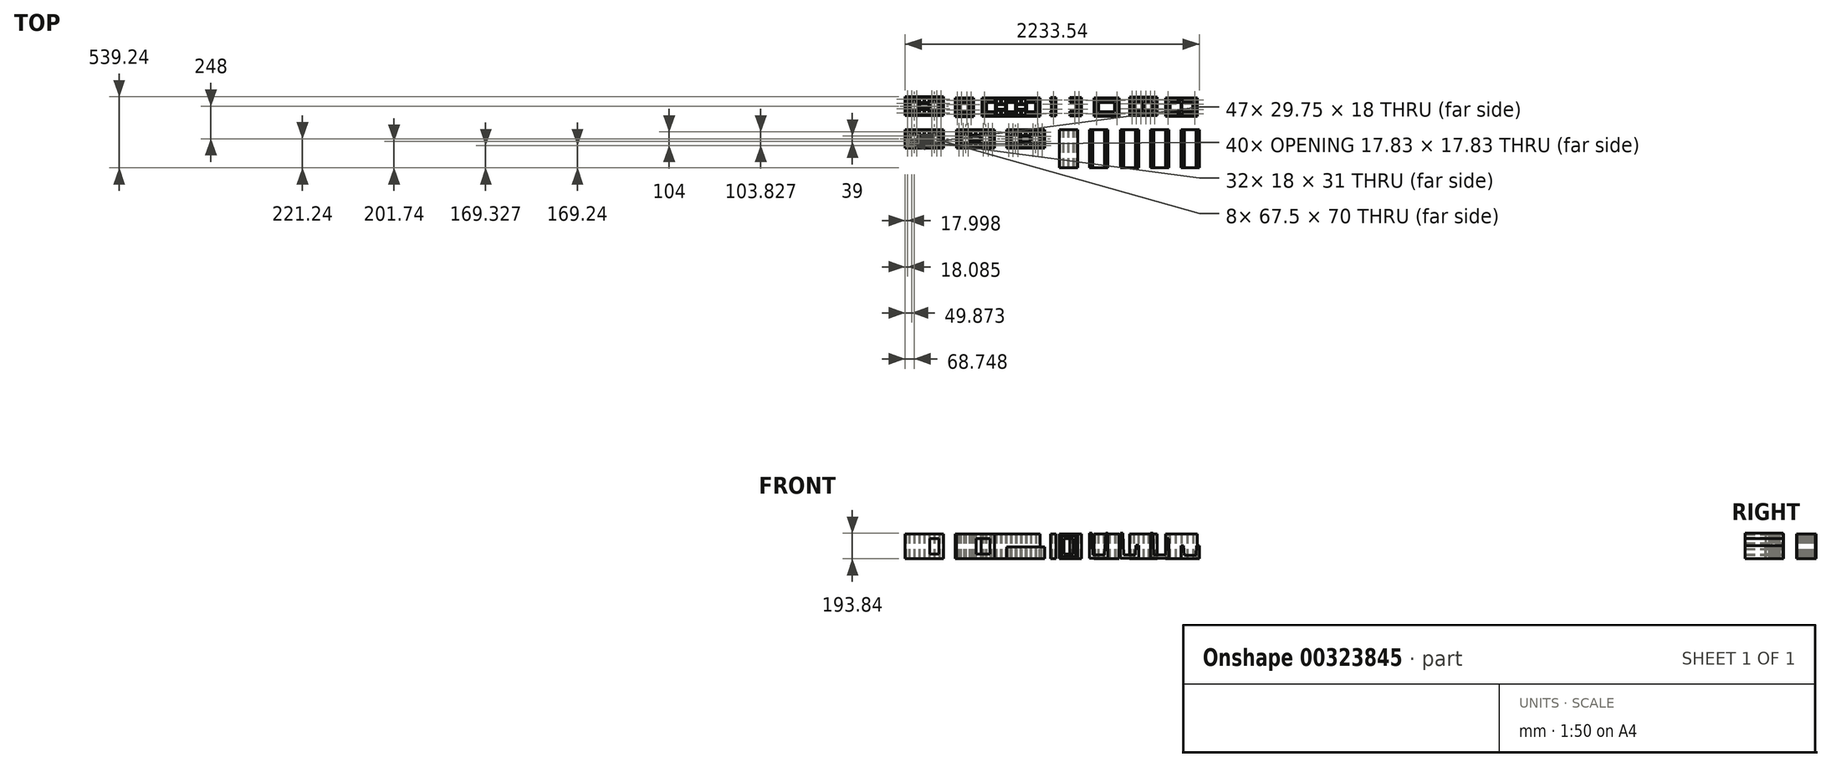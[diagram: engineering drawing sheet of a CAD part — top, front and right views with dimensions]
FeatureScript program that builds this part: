
annotation { "Feature Type Name" : "Feature", "Feature Type Description" : "" }
export const myFeature = defineFeature(function(context is Context, id is Id, definition is map)
    precondition{}
    {
        {
            var Q0;
            Q0=qCreatedBy(makeId("Top.planeOp"),FACE);
            var sketch = newSketch(context, id + "F0", { "sketchPlane" : qUnion([Q0])});
            skLineSegment(sketch, "E0", {"start": v(-1124.68, 173) * mm, "end": v(-1124.68, 33) * mm});
            skLineSegment(sketch, "E1", {"start": v(-1124.68, 33) * mm, "end": v(-834.68, 33) * mm});
            skLineSegment(sketch, "E2", {"start": v(-834.68, 33) * mm, "end": v(-834.68, 173) * mm});
            skLineSegment(sketch, "E3", {"start": v(-834.68, 173) * mm, "end": v(-1124.68, 173) * mm});
            skLineSegment(sketch, "E4", {"start": v(-1089.68, 164) * mm, "end": v(-1089.68, 146) * mm});
            skLineSegment(sketch, "E5", {"start": v(-1089.68, 146) * mm, "end": v(-1059.93, 146) * mm});
            skLineSegment(sketch, "E6", {"start": v(-1059.93, 146) * mm, "end": v(-1059.93, 164) * mm});
            skLineSegment(sketch, "E7", {"start": v(-1059.93, 164) * mm, "end": v(-1089.68, 164) * mm});
            skLineSegment(sketch, "E8", {"start": v(-1051.93, 164) * mm, "end": v(-1051.93, 146) * mm});
            skLineSegment(sketch, "E9", {"start": v(-1051.93, 146) * mm, "end": v(-1022.18, 146) * mm});
            skLineSegment(sketch, "E10", {"start": v(-1022.18, 146) * mm, "end": v(-1022.18, 164) * mm});
            skLineSegment(sketch, "E11", {"start": v(-1022.18, 164) * mm, "end": v(-1051.93, 164) * mm});
            skLineSegment(sketch, "E12", {"start": v(-1014.18, 164) * mm, "end": v(-1014.18, 129) * mm});
            skLineSegment(sketch, "E13", {"start": v(-1014.18, 129) * mm, "end": v(-983.68, 129) * mm});
            skLineSegment(sketch, "E14", {"start": v(-983.68, 129) * mm, "end": v(-983.68, 164) * mm});
            skLineSegment(sketch, "E15", {"start": v(-983.68, 164) * mm, "end": v(-1014.18, 164) * mm});
            skLineSegment(sketch, "E16", {"start": v(-975.68, 164) * mm, "end": v(-975.68, 129) * mm});
            skLineSegment(sketch, "E17", {"start": v(-975.68, 129) * mm, "end": v(-945.18, 129) * mm});
            skLineSegment(sketch, "E18", {"start": v(-945.18, 129) * mm, "end": v(-945.18, 164) * mm});
            skLineSegment(sketch, "E19", {"start": v(-945.18, 164) * mm, "end": v(-975.68, 164) * mm});
            skLineSegment(sketch, "E20", {"start": v(-937.18, 164) * mm, "end": v(-937.18, 146) * mm});
            skLineSegment(sketch, "E21", {"start": v(-937.18, 146) * mm, "end": v(-907.43, 146) * mm});
            skLineSegment(sketch, "E22", {"start": v(-907.43, 146) * mm, "end": v(-907.43, 164) * mm});
            skLineSegment(sketch, "E23", {"start": v(-907.43, 164) * mm, "end": v(-937.18, 164) * mm});
            skLineSegment(sketch, "E24", {"start": v(-899.43, 164) * mm, "end": v(-899.43, 146) * mm});
            skLineSegment(sketch, "E25", {"start": v(-899.43, 146) * mm, "end": v(-869.68, 146) * mm});
            skLineSegment(sketch, "E26", {"start": v(-869.68, 146) * mm, "end": v(-869.68, 164) * mm});
            skLineSegment(sketch, "E27", {"start": v(-869.68, 164) * mm, "end": v(-899.43, 164) * mm});
            skLineSegment(sketch, "E28", {"start": v(-861.68, 138) * mm, "end": v(-861.68, 107) * mm});
            skLineSegment(sketch, "E29", {"start": v(-861.68, 107) * mm, "end": v(-843.68, 107) * mm});
            skLineSegment(sketch, "E30", {"start": v(-843.68, 107) * mm, "end": v(-843.68, 138) * mm});
            skLineSegment(sketch, "E31", {"start": v(-843.68, 138) * mm, "end": v(-861.68, 138) * mm});
            skLineSegment(sketch, "E32", {"start": v(-1089.68, 138) * mm, "end": v(-1089.68, 68) * mm});
            skLineSegment(sketch, "E33", {"start": v(-1089.68, 68) * mm, "end": v(-1022.18, 68) * mm});
            skLineSegment(sketch, "E34", {"start": v(-1022.18, 68) * mm, "end": v(-1022.18, 138) * mm});
            skLineSegment(sketch, "E35", {"start": v(-1022.18, 138) * mm, "end": v(-1089.68, 138) * mm});
            skLineSegment(sketch, "E36", {"start": v(-1115.68, 138) * mm, "end": v(-1115.68, 107) * mm});
            skLineSegment(sketch, "E37", {"start": v(-1115.68, 107) * mm, "end": v(-1097.68, 107) * mm});
            skLineSegment(sketch, "E38", {"start": v(-1097.68, 107) * mm, "end": v(-1097.68, 138) * mm});
            skLineSegment(sketch, "E39", {"start": v(-1097.68, 138) * mm, "end": v(-1115.68, 138) * mm});
            skLineSegment(sketch, "E40", {"start": v(-1115.68, 99) * mm, "end": v(-1115.68, 68) * mm});
            skLineSegment(sketch, "E41", {"start": v(-1115.68, 68) * mm, "end": v(-1097.68, 68) * mm});
            skLineSegment(sketch, "E42", {"start": v(-1097.68, 68) * mm, "end": v(-1097.68, 99) * mm});
            skLineSegment(sketch, "E43", {"start": v(-1097.68, 99) * mm, "end": v(-1115.68, 99) * mm});
            skLineSegment(sketch, "E44", {"start": v(-1089.68, 60) * mm, "end": v(-1089.68, 42) * mm});
            skLineSegment(sketch, "E45", {"start": v(-1089.68, 42) * mm, "end": v(-1059.93, 42) * mm});
            skLineSegment(sketch, "E46", {"start": v(-1059.93, 42) * mm, "end": v(-1059.93, 60) * mm});
            skLineSegment(sketch, "E47", {"start": v(-1059.93, 60) * mm, "end": v(-1089.68, 60) * mm});
            skLineSegment(sketch, "E48", {"start": v(-1051.93, 60) * mm, "end": v(-1051.93, 42) * mm});
            skLineSegment(sketch, "E49", {"start": v(-1051.93, 42) * mm, "end": v(-1022.18, 42) * mm});
            skLineSegment(sketch, "E50", {"start": v(-1022.18, 42) * mm, "end": v(-1022.18, 60) * mm});
            skLineSegment(sketch, "E51", {"start": v(-1022.18, 60) * mm, "end": v(-1051.93, 60) * mm});
            skLineSegment(sketch, "E52", {"start": v(-1014.18, 121) * mm, "end": v(-1014.18, 85) * mm});
            skLineSegment(sketch, "E53", {"start": v(-1014.18, 85) * mm, "end": v(-945.18, 85) * mm});
            skLineSegment(sketch, "E54", {"start": v(-945.18, 85) * mm, "end": v(-945.18, 121) * mm});
            skLineSegment(sketch, "E55", {"start": v(-945.18, 121) * mm, "end": v(-1014.18, 121) * mm});
            skLineSegment(sketch, "E56", {"start": v(-1014.18, 77) * mm, "end": v(-1014.18, 42) * mm});
            skLineSegment(sketch, "E57", {"start": v(-1014.18, 42) * mm, "end": v(-983.68, 42) * mm});
            skLineSegment(sketch, "E58", {"start": v(-983.68, 42) * mm, "end": v(-983.68, 77) * mm});
            skLineSegment(sketch, "E59", {"start": v(-983.68, 77) * mm, "end": v(-1014.18, 77) * mm});
            skLineSegment(sketch, "E60", {"start": v(-975.68, 77) * mm, "end": v(-975.68, 42) * mm});
            skLineSegment(sketch, "E61", {"start": v(-975.68, 42) * mm, "end": v(-945.18, 42) * mm});
            skLineSegment(sketch, "E62", {"start": v(-945.18, 42) * mm, "end": v(-945.18, 77) * mm});
            skLineSegment(sketch, "E63", {"start": v(-945.18, 77) * mm, "end": v(-975.68, 77) * mm});
            skLineSegment(sketch, "E64", {"start": v(-937.18, 138) * mm, "end": v(-937.18, 68) * mm});
            skLineSegment(sketch, "E65", {"start": v(-937.18, 68) * mm, "end": v(-869.68, 68) * mm});
            skLineSegment(sketch, "E66", {"start": v(-869.68, 68) * mm, "end": v(-869.68, 138) * mm});
            skLineSegment(sketch, "E67", {"start": v(-869.68, 138) * mm, "end": v(-937.18, 138) * mm});
            skLineSegment(sketch, "E68", {"start": v(-937.18, 60) * mm, "end": v(-937.18, 42) * mm});
            skLineSegment(sketch, "E69", {"start": v(-937.18, 42) * mm, "end": v(-907.43, 42) * mm});
            skLineSegment(sketch, "E70", {"start": v(-907.43, 42) * mm, "end": v(-907.43, 60) * mm});
            skLineSegment(sketch, "E71", {"start": v(-907.43, 60) * mm, "end": v(-937.18, 60) * mm});
            skLineSegment(sketch, "E72", {"start": v(-899.43, 60) * mm, "end": v(-899.43, 42) * mm});
            skLineSegment(sketch, "E73", {"start": v(-899.43, 42) * mm, "end": v(-869.68, 42) * mm});
            skLineSegment(sketch, "E74", {"start": v(-869.68, 42) * mm, "end": v(-869.68, 60) * mm});
            skLineSegment(sketch, "E75", {"start": v(-869.68, 60) * mm, "end": v(-899.43, 60) * mm});
            skLineSegment(sketch, "E76", {"start": v(-861.68, 99) * mm, "end": v(-861.68, 68) * mm});
            skLineSegment(sketch, "E77", {"start": v(-861.68, 68) * mm, "end": v(-843.68, 68) * mm});
            skLineSegment(sketch, "E78", {"start": v(-843.68, 68) * mm, "end": v(-843.68, 99) * mm});
            skLineSegment(sketch, "E79", {"start": v(-843.68, 99) * mm, "end": v(-861.68, 99) * mm});
            skLineSegment(sketch, "E80", {"start": v(-745.6, 163.5) * mm, "end": v(-745.6, 23.5) * mm});
            skLineSegment(sketch, "E81", {"start": v(-745.6, 23.5) * mm, "end": v(-605.6, 23.5) * mm});
            skLineSegment(sketch, "E82", {"start": v(-605.6, 23.5) * mm, "end": v(-605.6, 163.5) * mm});
            skLineSegment(sketch, "E83", {"start": v(-605.6, 163.5) * mm, "end": v(-745.6, 163.5) * mm});
            skLineSegment(sketch, "E84", {"start": v(-710.6, 154.5) * mm, "end": v(-710.6, 136.5) * mm});
            skLineSegment(sketch, "E85", {"start": v(-710.6, 136.5) * mm, "end": v(-680.86, 136.5) * mm});
            skLineSegment(sketch, "E86", {"start": v(-680.86, 136.5) * mm, "end": v(-680.86, 154.5) * mm});
            skLineSegment(sketch, "E87", {"start": v(-680.86, 154.5) * mm, "end": v(-710.6, 154.5) * mm});
            skLineSegment(sketch, "E88", {"start": v(-670.36, 154.5) * mm, "end": v(-670.36, 136.5) * mm});
            skLineSegment(sketch, "E89", {"start": v(-670.36, 136.5) * mm, "end": v(-640.6, 136.5) * mm});
            skLineSegment(sketch, "E90", {"start": v(-640.6, 136.5) * mm, "end": v(-640.6, 154.5) * mm});
            skLineSegment(sketch, "E91", {"start": v(-640.6, 154.5) * mm, "end": v(-670.36, 154.5) * mm});
            skLineSegment(sketch, "E92", {"start": v(-632.6, 128.5) * mm, "end": v(-632.6, 97.5) * mm});
            skLineSegment(sketch, "E93", {"start": v(-632.6, 97.5) * mm, "end": v(-614.6, 97.5) * mm});
            skLineSegment(sketch, "E94", {"start": v(-614.6, 97.5) * mm, "end": v(-614.6, 128.5) * mm});
            skLineSegment(sketch, "E95", {"start": v(-614.6, 128.5) * mm, "end": v(-632.6, 128.5) * mm});
            skLineSegment(sketch, "E96", {"start": v(-736.6, 128.5) * mm, "end": v(-736.6, 97.5) * mm});
            skLineSegment(sketch, "E97", {"start": v(-736.6, 97.5) * mm, "end": v(-718.6, 97.5) * mm});
            skLineSegment(sketch, "E98", {"start": v(-718.6, 97.5) * mm, "end": v(-718.6, 128.5) * mm});
            skLineSegment(sketch, "E99", {"start": v(-718.6, 128.5) * mm, "end": v(-736.6, 128.5) * mm});
            skLineSegment(sketch, "E100", {"start": v(-736.6, 89.5) * mm, "end": v(-736.6, 58.5) * mm});
            skLineSegment(sketch, "E101", {"start": v(-736.6, 58.5) * mm, "end": v(-718.6, 58.5) * mm});
            skLineSegment(sketch, "E102", {"start": v(-718.6, 58.5) * mm, "end": v(-718.6, 89.5) * mm});
            skLineSegment(sketch, "E103", {"start": v(-718.6, 89.5) * mm, "end": v(-736.6, 89.5) * mm});
            skLineSegment(sketch, "E104", {"start": v(-710.6, 128.5) * mm, "end": v(-710.6, 58.5) * mm});
            skLineSegment(sketch, "E105", {"start": v(-710.6, 58.5) * mm, "end": v(-640.6, 58.5) * mm});
            skLineSegment(sketch, "E106", {"start": v(-640.6, 58.5) * mm, "end": v(-640.6, 128.5) * mm});
            skLineSegment(sketch, "E107", {"start": v(-640.6, 128.5) * mm, "end": v(-710.6, 128.5) * mm});
            skLineSegment(sketch, "E108", {"start": v(-710.6, 50.5) * mm, "end": v(-710.6, 32.5) * mm});
            skLineSegment(sketch, "E109", {"start": v(-710.6, 32.5) * mm, "end": v(-680.86, 32.5) * mm});
            skLineSegment(sketch, "E110", {"start": v(-680.86, 32.5) * mm, "end": v(-680.86, 50.5) * mm});
            skLineSegment(sketch, "E111", {"start": v(-680.86, 50.5) * mm, "end": v(-710.6, 50.5) * mm});
            skLineSegment(sketch, "E112", {"start": v(-670.36, 50.5) * mm, "end": v(-670.36, 32.5) * mm});
            skLineSegment(sketch, "E113", {"start": v(-670.36, 32.5) * mm, "end": v(-640.6, 32.5) * mm});
            skLineSegment(sketch, "E114", {"start": v(-640.6, 32.5) * mm, "end": v(-640.6, 50.5) * mm});
            skLineSegment(sketch, "E115", {"start": v(-640.6, 50.5) * mm, "end": v(-670.36, 50.5) * mm});
            skLineSegment(sketch, "E116", {"start": v(-632.6, 89.5) * mm, "end": v(-632.6, 58.5) * mm});
            skLineSegment(sketch, "E117", {"start": v(-632.6, 58.5) * mm, "end": v(-614.6, 58.5) * mm});
            skLineSegment(sketch, "E118", {"start": v(-614.6, 58.5) * mm, "end": v(-614.6, 89.5) * mm});
            skLineSegment(sketch, "E119", {"start": v(-614.6, 89.5) * mm, "end": v(-632.6, 89.5) * mm});
            skLineSegment(sketch, "E120", {"start": v(-540.95, 165.99) * mm, "end": v(-540.95, 25.99) * mm});
            skLineSegment(sketch, "E121", {"start": v(-100.95, 25.99) * mm, "end": v(-100.95, 165.99) * mm});
            skLineSegment(sketch, "E122", {"start": v(-100.95, 165.99) * mm, "end": v(-540.95, 165.99) * mm});
            skLineSegment(sketch, "E123", {"start": v(-506.14, 156.99) * mm, "end": v(-506.14, 138.99) * mm});
            skLineSegment(sketch, "E124", {"start": v(-506.14, 138.99) * mm, "end": v(-476.56, 138.99) * mm});
            skLineSegment(sketch, "E125", {"start": v(-476.56, 138.99) * mm, "end": v(-476.56, 156.99) * mm});
            skLineSegment(sketch, "E126", {"start": v(-476.56, 156.99) * mm, "end": v(-506.14, 156.99) * mm});
            skLineSegment(sketch, "E127", {"start": v(-468.6, 156.99) * mm, "end": v(-468.6, 138.99) * mm});
            skLineSegment(sketch, "E128", {"start": v(-468.6, 138.99) * mm, "end": v(-439.03, 138.99) * mm});
            skLineSegment(sketch, "E129", {"start": v(-439.03, 138.99) * mm, "end": v(-439.03, 156.99) * mm});
            skLineSegment(sketch, "E130", {"start": v(-439.03, 156.99) * mm, "end": v(-468.6, 156.99) * mm});
            skLineSegment(sketch, "E131", {"start": v(-532, 130.99) * mm, "end": v(-532, 99.99) * mm});
            skLineSegment(sketch, "E132", {"start": v(-532, 99.99) * mm, "end": v(-514.1, 99.99) * mm});
            skLineSegment(sketch, "E133", {"start": v(-514.1, 99.99) * mm, "end": v(-514.1, 130.99) * mm});
            skLineSegment(sketch, "E134", {"start": v(-514.1, 130.99) * mm, "end": v(-532, 130.99) * mm});
            skLineSegment(sketch, "E135", {"start": v(-532, 91.99) * mm, "end": v(-532, 60.99) * mm});
            skLineSegment(sketch, "E136", {"start": v(-532, 60.99) * mm, "end": v(-514.1, 60.99) * mm});
            skLineSegment(sketch, "E137", {"start": v(-514.1, 60.99) * mm, "end": v(-514.1, 91.99) * mm});
            skLineSegment(sketch, "E138", {"start": v(-514.1, 91.99) * mm, "end": v(-532, 91.99) * mm});
            skLineSegment(sketch, "E139", {"start": v(-506.14, 52.99) * mm, "end": v(-506.14, 34.99) * mm});
            skLineSegment(sketch, "E140", {"start": v(-506.14, 34.99) * mm, "end": v(-476.56, 34.99) * mm});
            skLineSegment(sketch, "E141", {"start": v(-476.56, 34.99) * mm, "end": v(-476.56, 52.99) * mm});
            skLineSegment(sketch, "E142", {"start": v(-476.56, 52.99) * mm, "end": v(-506.14, 52.99) * mm});
            skLineSegment(sketch, "E143", {"start": v(-468.6, 52.99) * mm, "end": v(-468.6, 34.99) * mm});
            skLineSegment(sketch, "E144", {"start": v(-468.6, 34.99) * mm, "end": v(-439.03, 34.99) * mm});
            skLineSegment(sketch, "E145", {"start": v(-439.03, 34.99) * mm, "end": v(-439.03, 52.99) * mm});
            skLineSegment(sketch, "E146", {"start": v(-439.03, 52.99) * mm, "end": v(-468.6, 52.99) * mm});
            skLineSegment(sketch, "E147", {"start": v(-431.07, 156.99) * mm, "end": v(-431.07, 121.99) * mm});
            skLineSegment(sketch, "E148", {"start": v(-431.07, 121.99) * mm, "end": v(-400.74, 121.99) * mm});
            skLineSegment(sketch, "E149", {"start": v(-400.74, 121.99) * mm, "end": v(-400.74, 156.99) * mm});
            skLineSegment(sketch, "E150", {"start": v(-400.74, 156.99) * mm, "end": v(-431.07, 156.99) * mm});
            skLineSegment(sketch, "E151", {"start": v(-392.79, 156.99) * mm, "end": v(-392.79, 121.99) * mm});
            skLineSegment(sketch, "E152", {"start": v(-392.79, 121.99) * mm, "end": v(-362.46, 121.99) * mm});
            skLineSegment(sketch, "E153", {"start": v(-362.46, 121.99) * mm, "end": v(-362.46, 156.99) * mm});
            skLineSegment(sketch, "E154", {"start": v(-362.46, 156.99) * mm, "end": v(-392.79, 156.99) * mm});
            skLineSegment(sketch, "E155", {"start": v(-431.07, 113.99) * mm, "end": v(-431.07, 77.99) * mm});
            skLineSegment(sketch, "E156", {"start": v(-431.07, 77.99) * mm, "end": v(-362.46, 77.99) * mm});
            skLineSegment(sketch, "E157", {"start": v(-362.46, 77.99) * mm, "end": v(-362.46, 113.99) * mm});
            skLineSegment(sketch, "E158", {"start": v(-362.46, 113.99) * mm, "end": v(-431.07, 113.99) * mm});
            skLineSegment(sketch, "E159", {"start": v(-431.07, 69.99) * mm, "end": v(-431.07, 34.99) * mm});
            skLineSegment(sketch, "E160", {"start": v(-431.07, 34.99) * mm, "end": v(-400.74, 34.99) * mm});
            skLineSegment(sketch, "E161", {"start": v(-400.74, 34.99) * mm, "end": v(-400.74, 69.99) * mm});
            skLineSegment(sketch, "E162", {"start": v(-400.74, 69.99) * mm, "end": v(-431.07, 69.99) * mm});
            skLineSegment(sketch, "E163", {"start": v(-392.79, 69.99) * mm, "end": v(-392.79, 34.99) * mm});
            skLineSegment(sketch, "E164", {"start": v(-392.79, 34.99) * mm, "end": v(-362.46, 34.99) * mm});
            skLineSegment(sketch, "E165", {"start": v(-362.46, 34.99) * mm, "end": v(-362.46, 69.99) * mm});
            skLineSegment(sketch, "E166", {"start": v(-362.46, 69.99) * mm, "end": v(-392.79, 69.99) * mm});
            skLineSegment(sketch, "E167", {"start": v(-506.14, 130.99) * mm, "end": v(-506.14, 60.99) * mm});
            skLineSegment(sketch, "E168", {"start": v(-506.14, 60.99) * mm, "end": v(-439.03, 60.99) * mm});
            skLineSegment(sketch, "E169", {"start": v(-439.03, 60.99) * mm, "end": v(-439.03, 130.99) * mm});
            skLineSegment(sketch, "E170", {"start": v(-439.03, 130.99) * mm, "end": v(-506.14, 130.99) * mm});
            skLineSegment(sketch, "E171", {"start": v(-354.5, 156.99) * mm, "end": v(-354.5, 138.99) * mm});
            skLineSegment(sketch, "E172", {"start": v(-354.5, 138.99) * mm, "end": v(-324.92, 138.99) * mm});
            skLineSegment(sketch, "E173", {"start": v(-324.92, 138.99) * mm, "end": v(-324.92, 156.99) * mm});
            skLineSegment(sketch, "E174", {"start": v(-324.92, 156.99) * mm, "end": v(-354.5, 156.99) * mm});
            skLineSegment(sketch, "E175", {"start": v(-316.97, 156.99) * mm, "end": v(-316.97, 138.99) * mm});
            skLineSegment(sketch, "E176", {"start": v(-316.97, 138.99) * mm, "end": v(-287.39, 138.99) * mm});
            skLineSegment(sketch, "E177", {"start": v(-287.39, 138.99) * mm, "end": v(-287.39, 156.99) * mm});
            skLineSegment(sketch, "E178", {"start": v(-287.39, 156.99) * mm, "end": v(-316.97, 156.99) * mm});
            skLineSegment(sketch, "E179", {"start": v(-279.43, 156.99) * mm, "end": v(-279.43, 121.99) * mm});
            skLineSegment(sketch, "E180", {"start": v(-279.43, 121.99) * mm, "end": v(-249.1, 121.99) * mm});
            skLineSegment(sketch, "E181", {"start": v(-249.1, 121.99) * mm, "end": v(-249.1, 156.99) * mm});
            skLineSegment(sketch, "E182", {"start": v(-249.1, 156.99) * mm, "end": v(-279.43, 156.99) * mm});
            skLineSegment(sketch, "E183", {"start": v(-241.15, 156.99) * mm, "end": v(-241.15, 121.99) * mm});
            skLineSegment(sketch, "E184", {"start": v(-241.15, 121.99) * mm, "end": v(-210.82, 121.99) * mm});
            skLineSegment(sketch, "E185", {"start": v(-210.82, 121.99) * mm, "end": v(-210.82, 156.99) * mm});
            skLineSegment(sketch, "E186", {"start": v(-210.82, 156.99) * mm, "end": v(-241.15, 156.99) * mm});
            skLineSegment(sketch, "E187", {"start": v(-202.87, 156.99) * mm, "end": v(-202.87, 138.99) * mm});
            skLineSegment(sketch, "E188", {"start": v(-202.87, 138.99) * mm, "end": v(-173.29, 138.99) * mm});
            skLineSegment(sketch, "E189", {"start": v(-173.29, 138.99) * mm, "end": v(-173.29, 156.99) * mm});
            skLineSegment(sketch, "E190", {"start": v(-173.29, 156.99) * mm, "end": v(-202.87, 156.99) * mm});
            skLineSegment(sketch, "E191", {"start": v(-165.33, 156.99) * mm, "end": v(-165.33, 138.99) * mm});
            skLineSegment(sketch, "E192", {"start": v(-165.33, 138.99) * mm, "end": v(-135.75, 138.99) * mm});
            skLineSegment(sketch, "E193", {"start": v(-135.75, 138.99) * mm, "end": v(-135.75, 156.99) * mm});
            skLineSegment(sketch, "E194", {"start": v(-135.75, 156.99) * mm, "end": v(-165.33, 156.99) * mm});
            skLineSegment(sketch, "E195", {"start": v(-354.5, 130.99) * mm, "end": v(-354.5, 60.99) * mm});
            skLineSegment(sketch, "E196", {"start": v(-354.5, 60.99) * mm, "end": v(-287.39, 60.99) * mm});
            skLineSegment(sketch, "E197", {"start": v(-287.39, 60.99) * mm, "end": v(-287.39, 130.99) * mm});
            skLineSegment(sketch, "E198", {"start": v(-287.39, 130.99) * mm, "end": v(-354.5, 130.99) * mm});
            skLineSegment(sketch, "E199", {"start": v(-354.5, 52.99) * mm, "end": v(-354.5, 34.99) * mm});
            skLineSegment(sketch, "E200", {"start": v(-354.5, 34.99) * mm, "end": v(-324.92, 34.99) * mm});
            skLineSegment(sketch, "E201", {"start": v(-324.92, 34.99) * mm, "end": v(-324.92, 52.99) * mm});
            skLineSegment(sketch, "E202", {"start": v(-324.92, 52.99) * mm, "end": v(-354.5, 52.99) * mm});
            skLineSegment(sketch, "E203", {"start": v(-316.97, 52.99) * mm, "end": v(-316.97, 34.99) * mm});
            skLineSegment(sketch, "E204", {"start": v(-316.97, 34.99) * mm, "end": v(-287.39, 34.99) * mm});
            skLineSegment(sketch, "E205", {"start": v(-287.39, 34.99) * mm, "end": v(-287.39, 52.99) * mm});
            skLineSegment(sketch, "E206", {"start": v(-287.39, 52.99) * mm, "end": v(-316.97, 52.99) * mm});
            skLineSegment(sketch, "E207", {"start": v(-279.43, 69.99) * mm, "end": v(-279.43, 34.99) * mm});
            skLineSegment(sketch, "E208", {"start": v(-279.43, 34.99) * mm, "end": v(-249.1, 34.99) * mm});
            skLineSegment(sketch, "E209", {"start": v(-249.1, 34.99) * mm, "end": v(-249.1, 69.99) * mm});
            skLineSegment(sketch, "E210", {"start": v(-249.1, 69.99) * mm, "end": v(-279.43, 69.99) * mm});
            skLineSegment(sketch, "E211", {"start": v(-279.43, 113.99) * mm, "end": v(-279.43, 77.99) * mm});
            skLineSegment(sketch, "E212", {"start": v(-279.43, 77.99) * mm, "end": v(-210.82, 77.99) * mm});
            skLineSegment(sketch, "E213", {"start": v(-210.82, 77.99) * mm, "end": v(-210.82, 113.99) * mm});
            skLineSegment(sketch, "E214", {"start": v(-210.82, 113.99) * mm, "end": v(-279.43, 113.99) * mm});
            skLineSegment(sketch, "E215", {"start": v(-241.15, 69.99) * mm, "end": v(-241.15, 34.99) * mm});
            skLineSegment(sketch, "E216", {"start": v(-241.15, 34.99) * mm, "end": v(-210.82, 34.99) * mm});
            skLineSegment(sketch, "E217", {"start": v(-210.82, 34.99) * mm, "end": v(-210.82, 69.99) * mm});
            skLineSegment(sketch, "E218", {"start": v(-210.82, 69.99) * mm, "end": v(-241.15, 69.99) * mm});
            skLineSegment(sketch, "E219", {"start": v(-202.87, 130.99) * mm, "end": v(-202.87, 60.99) * mm});
            skLineSegment(sketch, "E220", {"start": v(-202.87, 60.99) * mm, "end": v(-135.75, 60.99) * mm});
            skLineSegment(sketch, "E221", {"start": v(-135.75, 60.99) * mm, "end": v(-135.75, 130.99) * mm});
            skLineSegment(sketch, "E222", {"start": v(-135.75, 130.99) * mm, "end": v(-202.87, 130.99) * mm});
            skLineSegment(sketch, "E223", {"start": v(-202.87, 52.99) * mm, "end": v(-202.87, 34.99) * mm});
            skLineSegment(sketch, "E224", {"start": v(-202.87, 34.99) * mm, "end": v(-173.29, 34.99) * mm});
            skLineSegment(sketch, "E225", {"start": v(-173.29, 34.99) * mm, "end": v(-173.29, 52.99) * mm});
            skLineSegment(sketch, "E226", {"start": v(-173.29, 52.99) * mm, "end": v(-202.87, 52.99) * mm});
            skLineSegment(sketch, "E227", {"start": v(-165.33, 52.99) * mm, "end": v(-165.33, 34.99) * mm});
            skLineSegment(sketch, "E228", {"start": v(-165.33, 34.99) * mm, "end": v(-135.75, 34.99) * mm});
            skLineSegment(sketch, "E229", {"start": v(-135.75, 34.99) * mm, "end": v(-135.75, 52.99) * mm});
            skLineSegment(sketch, "E230", {"start": v(-135.75, 52.99) * mm, "end": v(-165.33, 52.99) * mm});
            skLineSegment(sketch, "E231", {"start": v(-127.8, 130.99) * mm, "end": v(-127.8, 99.99) * mm});
            skLineSegment(sketch, "E232", {"start": v(-127.8, 99.99) * mm, "end": v(-109.9, 99.99) * mm});
            skLineSegment(sketch, "E233", {"start": v(-109.9, 99.99) * mm, "end": v(-109.9, 130.99) * mm});
            skLineSegment(sketch, "E234", {"start": v(-109.9, 130.99) * mm, "end": v(-127.8, 130.99) * mm});
            skLineSegment(sketch, "E235", {"start": v(-109.9, 91.99) * mm, "end": v(-109.9, 60.99) * mm});
            skLineSegment(sketch, "E236", {"start": v(-109.9, 60.99) * mm, "end": v(-127.8, 60.99) * mm});
            skLineSegment(sketch, "E237", {"start": v(-127.8, 60.99) * mm, "end": v(-127.8, 91.99) * mm});
            skLineSegment(sketch, "E238", {"start": v(-127.8, 91.99) * mm, "end": v(-109.9, 91.99) * mm});
            skLineSegment(sketch, "E239", {"start": v(-6.9, 133.72) * mm, "end": v(-6.9, 102.72) * mm});
            skLineSegment(sketch, "E240", {"start": v(-6.9, 102.72) * mm, "end": v(11.1, 102.72) * mm});
            skLineSegment(sketch, "E241", {"start": v(11.1, 102.72) * mm, "end": v(11.1, 133.72) * mm});
            skLineSegment(sketch, "E242", {"start": v(11.1, 133.72) * mm, "end": v(-6.9, 133.72) * mm});
            skLineSegment(sketch, "E243", {"start": v(-6.9, 94.72) * mm, "end": v(-6.9, 63.72) * mm});
            skLineSegment(sketch, "E244", {"start": v(-6.9, 63.72) * mm, "end": v(11.1, 63.72) * mm});
            skLineSegment(sketch, "E245", {"start": v(11.1, 63.72) * mm, "end": v(11.1, 94.72) * mm});
            skLineSegment(sketch, "E246", {"start": v(11.1, 94.72) * mm, "end": v(-6.9, 94.72) * mm});
            skLineSegment(sketch, "E247", {"start": v(-19.9, 168.72) * mm, "end": v(20.1, 168.72) * mm});
            skLineSegment(sketch, "E248", {"start": v(20.1, 168.72) * mm, "end": v(20.1, 28.72) * mm});
            skLineSegment(sketch, "E249", {"start": v(20.1, 28.72) * mm, "end": v(-19.9, 28.72) * mm});
            skLineSegment(sketch, "E250", {"start": v(-19.9, 28.72) * mm, "end": v(-19.9, 37.72) * mm});
            skLineSegment(sketch, "E251", {"start": v(-19.9, 37.72) * mm, "end": v(-14.9, 37.72) * mm});
            skLineSegment(sketch, "E252", {"start": v(-14.9, 37.72) * mm, "end": v(-14.9, 55.72) * mm});
            skLineSegment(sketch, "E253", {"start": v(-14.9, 55.72) * mm, "end": v(-19.9, 55.72) * mm});
            skLineSegment(sketch, "E254", {"start": v(-19.9, 55.72) * mm, "end": v(-19.9, 63.72) * mm});
            skLineSegment(sketch, "E255", {"start": v(-19.9, 63.72) * mm, "end": v(-14.9, 63.72) * mm});
            skLineSegment(sketch, "E256", {"start": v(-14.9, 63.72) * mm, "end": v(-14.9, 133.72) * mm});
            skLineSegment(sketch, "E257", {"start": v(-14.9, 133.72) * mm, "end": v(-19.9, 133.72) * mm});
            skLineSegment(sketch, "E258", {"start": v(-19.9, 133.72) * mm, "end": v(-19.9, 141.72) * mm});
            skLineSegment(sketch, "E259", {"start": v(-19.9, 141.72) * mm, "end": v(-14.9, 141.72) * mm});
            skLineSegment(sketch, "E260", {"start": v(-14.9, 141.72) * mm, "end": v(-14.9, 159.72) * mm});
            skLineSegment(sketch, "E261", {"start": v(-14.9, 159.72) * mm, "end": v(-19.9, 159.72) * mm});
            skLineSegment(sketch, "E262", {"start": v(-19.9, 159.72) * mm, "end": v(-19.9, 168.72) * mm});
            skLineSegment(sketch, "E263", {"start": v(123.75, 168) * mm, "end": v(213.75, 168) * mm});
            skLineSegment(sketch, "E264", {"start": v(213.75, 168) * mm, "end": v(213.75, 28) * mm});
            skLineSegment(sketch, "E265", {"start": v(213.75, 28) * mm, "end": v(123.75, 28) * mm});
            skLineSegment(sketch, "E266", {"start": v(123.75, 28) * mm, "end": v(123.75, 37) * mm});
            skLineSegment(sketch, "E267", {"start": v(123.75, 37) * mm, "end": v(141, 37) * mm});
            skLineSegment(sketch, "E268", {"start": v(141, 37) * mm, "end": v(141, 55) * mm});
            skLineSegment(sketch, "E269", {"start": v(141, 55) * mm, "end": v(123.75, 55) * mm});
            skLineSegment(sketch, "E270", {"start": v(123.75, 55) * mm, "end": v(123.75, 63) * mm});
            skLineSegment(sketch, "E271", {"start": v(123.75, 63) * mm, "end": v(178.75, 63) * mm});
            skLineSegment(sketch, "E272", {"start": v(178.75, 63) * mm, "end": v(178.75, 133) * mm});
            skLineSegment(sketch, "E273", {"start": v(178.75, 133) * mm, "end": v(123.75, 133) * mm});
            skLineSegment(sketch, "E274", {"start": v(123.75, 133) * mm, "end": v(123.75, 141) * mm});
            skLineSegment(sketch, "E275", {"start": v(123.75, 141) * mm, "end": v(141, 141) * mm});
            skLineSegment(sketch, "E276", {"start": v(141, 141) * mm, "end": v(141, 159) * mm});
            skLineSegment(sketch, "E277", {"start": v(141, 159) * mm, "end": v(123.75, 159) * mm});
            skLineSegment(sketch, "E278", {"start": v(123.75, 159) * mm, "end": v(123.75, 168) * mm});
            skLineSegment(sketch, "E279", {"start": v(149, 159) * mm, "end": v(149, 141) * mm});
            skLineSegment(sketch, "E280", {"start": v(149, 141) * mm, "end": v(178.75, 141) * mm});
            skLineSegment(sketch, "E281", {"start": v(178.75, 141) * mm, "end": v(178.75, 159) * mm});
            skLineSegment(sketch, "E282", {"start": v(178.75, 159) * mm, "end": v(149, 159) * mm});
            skLineSegment(sketch, "E283", {"start": v(186.75, 133) * mm, "end": v(186.75, 102) * mm});
            skLineSegment(sketch, "E284", {"start": v(186.75, 102) * mm, "end": v(204.75, 102) * mm});
            skLineSegment(sketch, "E285", {"start": v(204.75, 102) * mm, "end": v(204.75, 133) * mm});
            skLineSegment(sketch, "E286", {"start": v(204.75, 133) * mm, "end": v(186.75, 133) * mm});
            skLineSegment(sketch, "E287", {"start": v(204.75, 94) * mm, "end": v(204.75, 63) * mm});
            skLineSegment(sketch, "E288", {"start": v(204.75, 63) * mm, "end": v(186.75, 63) * mm});
            skLineSegment(sketch, "E289", {"start": v(186.75, 63) * mm, "end": v(186.75, 94) * mm});
            skLineSegment(sketch, "E290", {"start": v(186.75, 94) * mm, "end": v(204.75, 94) * mm});
            skLineSegment(sketch, "E291", {"start": v(149, 55) * mm, "end": v(149, 37) * mm});
            skLineSegment(sketch, "E292", {"start": v(149, 37) * mm, "end": v(178.75, 37) * mm});
            skLineSegment(sketch, "E293", {"start": v(178.75, 37) * mm, "end": v(178.75, 55) * mm});
            skLineSegment(sketch, "E294", {"start": v(178.75, 55) * mm, "end": v(149, 55) * mm});
            skLineSegment(sketch, "E295", {"start": v(310.8, 164.82) * mm, "end": v(310.8, 24.82) * mm});
            skLineSegment(sketch, "E296", {"start": v(310.8, 24.82) * mm, "end": v(500.8, 24.82) * mm});
            skLineSegment(sketch, "E297", {"start": v(500.8, 24.82) * mm, "end": v(500.8, 164.82) * mm});
            skLineSegment(sketch, "E298", {"start": v(500.8, 164.82) * mm, "end": v(310.8, 164.82) * mm});
            skLineSegment(sketch, "E299", {"start": v(345.8, 155.82) * mm, "end": v(345.8, 137.82) * mm});
            skLineSegment(sketch, "E300", {"start": v(345.8, 137.82) * mm, "end": v(380.46, 137.82) * mm});
            skLineSegment(sketch, "E301", {"start": v(380.46, 137.82) * mm, "end": v(380.46, 155.82) * mm});
            skLineSegment(sketch, "E302", {"start": v(380.46, 155.82) * mm, "end": v(345.8, 155.82) * mm});
            skLineSegment(sketch, "E303", {"start": v(388.46, 155.82) * mm, "end": v(388.46, 137.82) * mm});
            skLineSegment(sketch, "E304", {"start": v(388.46, 137.82) * mm, "end": v(423.13, 137.82) * mm});
            skLineSegment(sketch, "E305", {"start": v(423.13, 137.82) * mm, "end": v(423.13, 155.82) * mm});
            skLineSegment(sketch, "E306", {"start": v(423.13, 155.82) * mm, "end": v(388.46, 155.82) * mm});
            skLineSegment(sketch, "E307", {"start": v(431.13, 137.82) * mm, "end": v(431.13, 155.82) * mm});
            skLineSegment(sketch, "E308", {"start": v(431.13, 155.82) * mm, "end": v(465.8, 155.82) * mm});
            skLineSegment(sketch, "E309", {"start": v(465.8, 155.82) * mm, "end": v(465.8, 137.82) * mm});
            skLineSegment(sketch, "E310", {"start": v(465.8, 137.82) * mm, "end": v(431.13, 137.82) * mm});
            skLineSegment(sketch, "E311", {"start": v(319.8, 129.82) * mm, "end": v(319.8, 99.82) * mm});
            skLineSegment(sketch, "E312", {"start": v(319.8, 99.82) * mm, "end": v(337.8, 99.82) * mm});
            skLineSegment(sketch, "E313", {"start": v(337.8, 99.82) * mm, "end": v(337.8, 129.82) * mm});
            skLineSegment(sketch, "E314", {"start": v(337.8, 129.82) * mm, "end": v(319.8, 129.82) * mm});
            skLineSegment(sketch, "E315", {"start": v(337.8, 89.82) * mm, "end": v(337.8, 59.82) * mm});
            skLineSegment(sketch, "E316", {"start": v(337.8, 59.82) * mm, "end": v(319.8, 59.82) * mm});
            skLineSegment(sketch, "E317", {"start": v(319.8, 59.82) * mm, "end": v(319.8, 89.82) * mm});
            skLineSegment(sketch, "E318", {"start": v(319.8, 89.82) * mm, "end": v(337.8, 89.82) * mm});
            skLineSegment(sketch, "E319", {"start": v(345.8, 51.82) * mm, "end": v(345.8, 33.82) * mm});
            skLineSegment(sketch, "E320", {"start": v(345.8, 33.82) * mm, "end": v(380.46, 33.82) * mm});
            skLineSegment(sketch, "E321", {"start": v(380.46, 33.82) * mm, "end": v(380.46, 51.82) * mm});
            skLineSegment(sketch, "E322", {"start": v(380.46, 51.82) * mm, "end": v(345.8, 51.82) * mm});
            skLineSegment(sketch, "E323", {"start": v(388.46, 33.82) * mm, "end": v(388.46, 51.82) * mm});
            skLineSegment(sketch, "E324", {"start": v(388.46, 51.82) * mm, "end": v(423.13, 51.82) * mm});
            skLineSegment(sketch, "E325", {"start": v(423.13, 51.82) * mm, "end": v(423.13, 33.82) * mm});
            skLineSegment(sketch, "E326", {"start": v(423.13, 33.82) * mm, "end": v(388.46, 33.82) * mm});
            skLineSegment(sketch, "E327", {"start": v(431.13, 51.82) * mm, "end": v(431.13, 33.82) * mm});
            skLineSegment(sketch, "E328", {"start": v(431.13, 33.82) * mm, "end": v(465.8, 33.82) * mm});
            skLineSegment(sketch, "E329", {"start": v(465.8, 33.82) * mm, "end": v(465.8, 51.82) * mm});
            skLineSegment(sketch, "E330", {"start": v(465.8, 51.82) * mm, "end": v(431.13, 51.82) * mm});
            skLineSegment(sketch, "E331", {"start": v(345.8, 129.82) * mm, "end": v(345.8, 59.82) * mm});
            skLineSegment(sketch, "E332", {"start": v(345.8, 59.82) * mm, "end": v(465.8, 59.82) * mm});
            skLineSegment(sketch, "E333", {"start": v(465.8, 59.82) * mm, "end": v(465.8, 129.82) * mm});
            skLineSegment(sketch, "E334", {"start": v(465.8, 129.82) * mm, "end": v(345.8, 129.82) * mm});
            skLineSegment(sketch, "E335", {"start": v(473.8, 129.82) * mm, "end": v(473.8, 99.82) * mm});
            skLineSegment(sketch, "E336", {"start": v(473.8, 99.82) * mm, "end": v(491.8, 99.82) * mm});
            skLineSegment(sketch, "E337", {"start": v(491.8, 99.82) * mm, "end": v(491.8, 129.82) * mm});
            skLineSegment(sketch, "E338", {"start": v(491.8, 129.82) * mm, "end": v(473.8, 129.82) * mm});
            skLineSegment(sketch, "E339", {"start": v(473.8, 89.82) * mm, "end": v(473.8, 59.82) * mm});
            skLineSegment(sketch, "E340", {"start": v(473.8, 59.82) * mm, "end": v(491.8, 59.82) * mm});
            skLineSegment(sketch, "E341", {"start": v(491.8, 59.82) * mm, "end": v(491.8, 89.82) * mm});
            skLineSegment(sketch, "E342", {"start": v(491.8, 89.82) * mm, "end": v(473.8, 89.82) * mm});
            skLineSegment(sketch, "E343", {"start": v(579.39, 171.67) * mm, "end": v(579.39, 31.67) * mm});
            skLineSegment(sketch, "E344", {"start": v(579.39, 31.67) * mm, "end": v(789.39, 31.67) * mm});
            skLineSegment(sketch, "E345", {"start": v(789.39, 31.67) * mm, "end": v(789.39, 171.67) * mm});
            skLineSegment(sketch, "E346", {"start": v(789.39, 171.67) * mm, "end": v(579.39, 171.67) * mm});
            skLineSegment(sketch, "E347", {"start": v(614.39, 162.67) * mm, "end": v(614.39, 144.67) * mm});
            skLineSegment(sketch, "E348", {"start": v(614.39, 144.67) * mm, "end": v(644.14, 144.67) * mm});
            skLineSegment(sketch, "E349", {"start": v(644.14, 144.67) * mm, "end": v(644.14, 162.67) * mm});
            skLineSegment(sketch, "E350", {"start": v(644.14, 162.67) * mm, "end": v(614.39, 162.67) * mm});
            skLineSegment(sketch, "E351", {"start": v(614.39, 58.67) * mm, "end": v(614.39, 40.67) * mm});
            skLineSegment(sketch, "E352", {"start": v(614.39, 40.67) * mm, "end": v(644.14, 40.67) * mm});
            skLineSegment(sketch, "E353", {"start": v(644.14, 40.67) * mm, "end": v(644.14, 58.67) * mm});
            skLineSegment(sketch, "E354", {"start": v(644.14, 58.67) * mm, "end": v(614.39, 58.67) * mm});
            skLineSegment(sketch, "E355", {"start": v(588.39, 136.67) * mm, "end": v(588.39, 105.67) * mm});
            skLineSegment(sketch, "E356", {"start": v(588.39, 105.67) * mm, "end": v(606.39, 105.67) * mm});
            skLineSegment(sketch, "E357", {"start": v(606.39, 105.67) * mm, "end": v(606.39, 136.67) * mm});
            skLineSegment(sketch, "E358", {"start": v(606.39, 136.67) * mm, "end": v(588.39, 136.67) * mm});
            skLineSegment(sketch, "E359", {"start": v(650.64, 162.67) * mm, "end": v(650.64, 144.67) * mm});
            skLineSegment(sketch, "E360", {"start": v(650.64, 144.67) * mm, "end": v(680.39, 144.67) * mm});
            skLineSegment(sketch, "E361", {"start": v(680.39, 144.67) * mm, "end": v(680.39, 162.67) * mm});
            skLineSegment(sketch, "E362", {"start": v(680.39, 162.67) * mm, "end": v(650.64, 162.67) * mm});
            skLineSegment(sketch, "E363", {"start": v(688.39, 162.67) * mm, "end": v(688.39, 144.67) * mm});
            skLineSegment(sketch, "E364", {"start": v(688.39, 144.67) * mm, "end": v(718.14, 144.67) * mm});
            skLineSegment(sketch, "E365", {"start": v(718.14, 144.67) * mm, "end": v(718.14, 162.67) * mm});
            skLineSegment(sketch, "E366", {"start": v(718.14, 162.67) * mm, "end": v(688.39, 162.67) * mm});
            skLineSegment(sketch, "E367", {"start": v(724.64, 162.67) * mm, "end": v(724.64, 144.67) * mm});
            skLineSegment(sketch, "E368", {"start": v(724.64, 144.67) * mm, "end": v(754.39, 144.67) * mm});
            skLineSegment(sketch, "E369", {"start": v(754.39, 144.67) * mm, "end": v(754.39, 162.67) * mm});
            skLineSegment(sketch, "E370", {"start": v(754.39, 162.67) * mm, "end": v(724.64, 162.67) * mm});
            skLineSegment(sketch, "E371", {"start": v(650.64, 58.67) * mm, "end": v(650.64, 40.67) * mm});
            skLineSegment(sketch, "E372", {"start": v(650.64, 40.67) * mm, "end": v(680.39, 40.67) * mm});
            skLineSegment(sketch, "E373", {"start": v(680.39, 40.67) * mm, "end": v(680.39, 58.67) * mm});
            skLineSegment(sketch, "E374", {"start": v(680.39, 58.67) * mm, "end": v(650.64, 58.67) * mm});
            skLineSegment(sketch, "E375", {"start": v(688.39, 58.67) * mm, "end": v(688.39, 40.67) * mm});
            skLineSegment(sketch, "E376", {"start": v(688.39, 40.67) * mm, "end": v(718.14, 40.67) * mm});
            skLineSegment(sketch, "E377", {"start": v(718.14, 40.67) * mm, "end": v(718.14, 58.67) * mm});
            skLineSegment(sketch, "E378", {"start": v(718.14, 58.67) * mm, "end": v(688.39, 58.67) * mm});
            skLineSegment(sketch, "E379", {"start": v(724.64, 58.67) * mm, "end": v(724.64, 40.67) * mm});
            skLineSegment(sketch, "E380", {"start": v(724.64, 40.67) * mm, "end": v(754.39, 40.67) * mm});
            skLineSegment(sketch, "E381", {"start": v(754.39, 40.67) * mm, "end": v(754.39, 58.67) * mm});
            skLineSegment(sketch, "E382", {"start": v(754.39, 58.67) * mm, "end": v(724.64, 58.67) * mm});
            skLineSegment(sketch, "E383", {"start": v(588.39, 97.67) * mm, "end": v(588.39, 66.67) * mm});
            skLineSegment(sketch, "E384", {"start": v(588.39, 66.67) * mm, "end": v(606.39, 66.67) * mm});
            skLineSegment(sketch, "E385", {"start": v(606.39, 66.67) * mm, "end": v(606.39, 97.67) * mm});
            skLineSegment(sketch, "E386", {"start": v(606.39, 97.67) * mm, "end": v(588.39, 97.67) * mm});
            skLineSegment(sketch, "E387", {"start": v(762.39, 97.67) * mm, "end": v(762.39, 66.67) * mm});
            skLineSegment(sketch, "E388", {"start": v(762.39, 66.67) * mm, "end": v(780.39, 66.67) * mm});
            skLineSegment(sketch, "E389", {"start": v(780.39, 66.67) * mm, "end": v(780.39, 97.67) * mm});
            skLineSegment(sketch, "E390", {"start": v(780.39, 97.67) * mm, "end": v(762.39, 97.67) * mm});
            skLineSegment(sketch, "E391", {"start": v(762.39, 136.67) * mm, "end": v(762.39, 105.67) * mm});
            skLineSegment(sketch, "E392", {"start": v(762.39, 105.67) * mm, "end": v(780.39, 105.67) * mm});
            skLineSegment(sketch, "E393", {"start": v(780.39, 105.67) * mm, "end": v(780.39, 136.67) * mm});
            skLineSegment(sketch, "E394", {"start": v(780.39, 136.67) * mm, "end": v(762.39, 136.67) * mm});
            skLineSegment(sketch, "E395", {"start": v(614.39, 136.67) * mm, "end": v(614.39, 66.67) * mm});
            skLineSegment(sketch, "E396", {"start": v(614.39, 66.67) * mm, "end": v(680.39, 66.67) * mm});
            skLineSegment(sketch, "E397", {"start": v(680.39, 66.67) * mm, "end": v(680.39, 136.67) * mm});
            skLineSegment(sketch, "E398", {"start": v(680.39, 136.67) * mm, "end": v(614.39, 136.67) * mm});
            skLineSegment(sketch, "E399", {"start": v(688.39, 66.67) * mm, "end": v(688.39, 136.67) * mm});
            skLineSegment(sketch, "E400", {"start": v(688.39, 136.67) * mm, "end": v(754.39, 136.67) * mm});
            skLineSegment(sketch, "E401", {"start": v(754.39, 136.67) * mm, "end": v(754.39, 66.67) * mm});
            skLineSegment(sketch, "E402", {"start": v(754.39, 66.67) * mm, "end": v(688.39, 66.67) * mm});
            skLineSegment(sketch, "E403", {"start": v(852.51, 166.38) * mm, "end": v(852.51, 26.38) * mm});
            skLineSegment(sketch, "E404", {"start": v(852.51, 26.38) * mm, "end": v(1092.51, 26.38) * mm});
            skLineSegment(sketch, "E405", {"start": v(1092.51, 26.38) * mm, "end": v(1092.51, 166.38) * mm});
            skLineSegment(sketch, "E406", {"start": v(1092.51, 166.38) * mm, "end": v(852.51, 166.38) * mm});
            skLineSegment(sketch, "E407", {"start": v(976.51, 131.38) * mm, "end": v(976.51, 61.38) * mm});
            skLineSegment(sketch, "E408", {"start": v(976.51, 61.38) * mm, "end": v(1057.51, 61.38) * mm});
            skLineSegment(sketch, "E409", {"start": v(1057.51, 61.38) * mm, "end": v(1057.51, 131.38) * mm});
            skLineSegment(sketch, "E410", {"start": v(1057.51, 131.38) * mm, "end": v(976.51, 131.38) * mm});
            skLineSegment(sketch, "E411", {"start": v(887.51, 157.38) * mm, "end": v(887.51, 139.38) * mm});
            skLineSegment(sketch, "E412", {"start": v(887.51, 139.38) * mm, "end": v(924.01, 139.38) * mm});
            skLineSegment(sketch, "E413", {"start": v(924.01, 139.38) * mm, "end": v(924.01, 157.38) * mm});
            skLineSegment(sketch, "E414", {"start": v(924.01, 157.38) * mm, "end": v(887.51, 157.38) * mm});
            skLineSegment(sketch, "E415", {"start": v(861.51, 131.38) * mm, "end": v(861.51, 100.38) * mm});
            skLineSegment(sketch, "E416", {"start": v(861.51, 100.38) * mm, "end": v(879.51, 100.38) * mm});
            skLineSegment(sketch, "E417", {"start": v(879.51, 100.38) * mm, "end": v(879.51, 131.38) * mm});
            skLineSegment(sketch, "E418", {"start": v(879.51, 131.38) * mm, "end": v(861.51, 131.38) * mm});
            skLineSegment(sketch, "E419", {"start": v(861.51, 92.38) * mm, "end": v(861.51, 61.38) * mm});
            skLineSegment(sketch, "E420", {"start": v(861.51, 61.38) * mm, "end": v(879.51, 61.38) * mm});
            skLineSegment(sketch, "E421", {"start": v(879.51, 61.38) * mm, "end": v(879.51, 92.38) * mm});
            skLineSegment(sketch, "E422", {"start": v(879.51, 92.38) * mm, "end": v(861.51, 92.38) * mm});
            skLineSegment(sketch, "E423", {"start": v(1065.51, 131.38) * mm, "end": v(1065.51, 100.38) * mm});
            skLineSegment(sketch, "E424", {"start": v(1065.51, 100.38) * mm, "end": v(1083.51, 100.38) * mm});
            skLineSegment(sketch, "E425", {"start": v(1083.51, 100.38) * mm, "end": v(1083.51, 131.38) * mm});
            skLineSegment(sketch, "E426", {"start": v(1083.51, 131.38) * mm, "end": v(1065.51, 131.38) * mm});
            skLineSegment(sketch, "E427", {"start": v(1065.51, 92.38) * mm, "end": v(1065.51, 61.38) * mm});
            skLineSegment(sketch, "E428", {"start": v(1065.51, 61.38) * mm, "end": v(1083.51, 61.38) * mm});
            skLineSegment(sketch, "E429", {"start": v(1083.51, 61.38) * mm, "end": v(1083.51, 92.38) * mm});
            skLineSegment(sketch, "E430", {"start": v(1083.51, 92.38) * mm, "end": v(1065.51, 92.38) * mm});
            skLineSegment(sketch, "E431", {"start": v(932.01, 157.38) * mm, "end": v(932.01, 139.38) * mm});
            skLineSegment(sketch, "E432", {"start": v(932.01, 139.38) * mm, "end": v(968.51, 139.38) * mm});
            skLineSegment(sketch, "E433", {"start": v(968.51, 139.38) * mm, "end": v(968.51, 157.38) * mm});
            skLineSegment(sketch, "E434", {"start": v(968.51, 157.38) * mm, "end": v(932.01, 157.38) * mm});
            skLineSegment(sketch, "E435", {"start": v(976.51, 157.38) * mm, "end": v(976.51, 139.38) * mm});
            skLineSegment(sketch, "E436", {"start": v(976.51, 139.38) * mm, "end": v(1013.01, 139.38) * mm});
            skLineSegment(sketch, "E437", {"start": v(1013.01, 139.38) * mm, "end": v(1013.01, 157.38) * mm});
            skLineSegment(sketch, "E438", {"start": v(1013.01, 157.38) * mm, "end": v(976.51, 157.38) * mm});
            skLineSegment(sketch, "E439", {"start": v(1021.01, 157.38) * mm, "end": v(1021.01, 139.38) * mm});
            skLineSegment(sketch, "E440", {"start": v(1021.01, 139.38) * mm, "end": v(1057.51, 139.38) * mm});
            skLineSegment(sketch, "E441", {"start": v(1057.51, 139.38) * mm, "end": v(1057.51, 157.38) * mm});
            skLineSegment(sketch, "E442", {"start": v(1057.51, 157.38) * mm, "end": v(1021.01, 157.38) * mm});
            skLineSegment(sketch, "E443", {"start": v(887.51, 53.38) * mm, "end": v(887.51, 35.38) * mm});
            skLineSegment(sketch, "E444", {"start": v(887.51, 35.38) * mm, "end": v(924.01, 35.38) * mm});
            skLineSegment(sketch, "E445", {"start": v(924.01, 35.38) * mm, "end": v(924.01, 53.38) * mm});
            skLineSegment(sketch, "E446", {"start": v(924.01, 53.38) * mm, "end": v(887.51, 53.38) * mm});
            skLineSegment(sketch, "E447", {"start": v(932.01, 53.38) * mm, "end": v(932.01, 35.38) * mm});
            skLineSegment(sketch, "E448", {"start": v(932.01, 35.38) * mm, "end": v(968.51, 35.38) * mm});
            skLineSegment(sketch, "E449", {"start": v(968.51, 35.38) * mm, "end": v(968.51, 53.38) * mm});
            skLineSegment(sketch, "E450", {"start": v(968.51, 53.38) * mm, "end": v(932.01, 53.38) * mm});
            skLineSegment(sketch, "E451", {"start": v(976.51, 53.38) * mm, "end": v(976.51, 35.38) * mm});
            skLineSegment(sketch, "E452", {"start": v(976.51, 35.38) * mm, "end": v(1013.01, 35.38) * mm});
            skLineSegment(sketch, "E453", {"start": v(1013.01, 35.38) * mm, "end": v(1013.01, 53.38) * mm});
            skLineSegment(sketch, "E454", {"start": v(1013.01, 53.38) * mm, "end": v(976.51, 53.38) * mm});
            skLineSegment(sketch, "E455", {"start": v(1021.01, 53.38) * mm, "end": v(1021.01, 35.38) * mm});
            skLineSegment(sketch, "E456", {"start": v(1021.01, 35.38) * mm, "end": v(1057.51, 35.38) * mm});
            skLineSegment(sketch, "E457", {"start": v(1057.51, 35.38) * mm, "end": v(1057.51, 53.38) * mm});
            skLineSegment(sketch, "E458", {"start": v(1057.51, 53.38) * mm, "end": v(1021.01, 53.38) * mm});
            skLineSegment(sketch, "E459", {"start": v(887.51, 131.38) * mm, "end": v(887.51, 61.38) * mm});
            skLineSegment(sketch, "E460", {"start": v(887.51, 61.38) * mm, "end": v(968.51, 61.38) * mm});
            skLineSegment(sketch, "E461", {"start": v(968.51, 61.38) * mm, "end": v(968.51, 131.38) * mm});
            skLineSegment(sketch, "E462", {"start": v(968.51, 131.38) * mm, "end": v(887.51, 131.38) * mm});
            skArc(sketch, "E463.cCircle", {"start": v(-1097.68, 155) * mm, "mid": v(-1113.05, 161.36) * mm, "end": v(-1106.68, 146) * mm});
            skPoint(sketch, "E463.cCircle.centerSnap0", {"position": v(-1089.68, 155) * mm});
            skPoint(sketch, "E463.cCircle.centerSnap1", {"position": v(-1106.68, 138) * mm});
            skLineSegment(sketch, "E463.0", {"start": v(-1097.68, 146) * mm, "end": v(-1106.68, 146) * mm});
            skLineSegment(sketch, "E463.3", {"start": v(-1097.68, 155) * mm, "end": v(-1097.68, 146) * mm});
            skPoint(sketch, "E463.0.midPoint", {"position": v(-1106.68, 146) * mm});
            skArc(sketch, "E464.cCircle", {"start": v(-1106.68, 60) * mm, "mid": v(-1113.05, 44.64) * mm, "end": v(-1097.68, 51) * mm});
            skPoint(sketch, "E464.cCircle.centerSnap0", {"position": v(-1106.68, 68) * mm});
            skPoint(sketch, "E464.cCircle.centerSnap1", {"position": v(-1089.68, 51) * mm});
            skLineSegment(sketch, "E464.0", {"start": v(-1106.68, 60) * mm, "end": v(-1097.68, 60) * mm});
            skLineSegment(sketch, "E464.1", {"start": v(-1097.68, 60) * mm, "end": v(-1097.68, 51) * mm});
            skPoint(sketch, "E464.0.midPoint", {"position": v(-1106.68, 60) * mm});
            skArc(sketch, "E465.cCircle", {"start": v(-861.68, 51) * mm, "mid": v(-846.32, 44.64) * mm, "end": v(-852.68, 60) * mm});
            skPoint(sketch, "E465.cCircle.centerSnap0", {"position": v(-852.68, 68) * mm});
            skPoint(sketch, "E465.cCircle.centerSnap1", {"position": v(-869.68, 51) * mm});
            skLineSegment(sketch, "E465.0", {"start": v(-861.68, 60) * mm, "end": v(-852.68, 60) * mm});
            skLineSegment(sketch, "E465.3", {"start": v(-861.68, 51) * mm, "end": v(-861.68, 60) * mm});
            skPoint(sketch, "E465.0.midPoint", {"position": v(-852.68, 60) * mm});
            skArc(sketch, "E466.cCircle", {"start": v(-852.68, 146) * mm, "mid": v(-846.32, 161.36) * mm, "end": v(-861.68, 155) * mm});
            skPoint(sketch, "E466.cCircle.centerSnap0", {"position": v(-852.68, 138) * mm});
            skPoint(sketch, "E466.cCircle.centerSnap1", {"position": v(-869.68, 155) * mm});
            skLineSegment(sketch, "E466.0", {"start": v(-852.68, 146) * mm, "end": v(-861.68, 146) * mm});
            skLineSegment(sketch, "E466.1", {"start": v(-861.68, 146) * mm, "end": v(-861.68, 155) * mm});
            skPoint(sketch, "E466.0.midPoint", {"position": v(-852.68, 146) * mm});
            skArc(sketch, "E467.cCircle", {"start": v(-727.6, 50.5) * mm, "mid": v(-733.97, 35.14) * mm, "end": v(-718.6, 41.5) * mm});
            skPoint(sketch, "E467.cCircle.centerSnap0", {"position": v(-727.6, 58.5) * mm});
            skPoint(sketch, "E467.cCircle.centerSnap1", {"position": v(-710.6, 41.5) * mm});
            skLineSegment(sketch, "E467.0", {"start": v(-727.6, 50.5) * mm, "end": v(-718.6, 50.5) * mm});
            skLineSegment(sketch, "E467.1", {"start": v(-718.6, 50.5) * mm, "end": v(-718.6, 41.5) * mm});
            skPoint(sketch, "E467.0.midPoint", {"position": v(-727.6, 50.5) * mm});
            skArc(sketch, "E468.cCircle", {"start": v(-718.6, 145.5) * mm, "mid": v(-733.97, 151.87) * mm, "end": v(-727.6, 136.5) * mm});
            skPoint(sketch, "E468.cCircle.centerSnap0", {"position": v(-727.6, 128.5) * mm});
            skPoint(sketch, "E468.cCircle.centerSnap1", {"position": v(-710.6, 145.5) * mm});
            skLineSegment(sketch, "E468.0", {"start": v(-718.6, 136.5) * mm, "end": v(-727.6, 136.5) * mm});
            skLineSegment(sketch, "E468.3", {"start": v(-718.6, 145.5) * mm, "end": v(-718.6, 136.5) * mm});
            skPoint(sketch, "E468.0.midPoint", {"position": v(-727.6, 136.5) * mm});
            skArc(sketch, "E469.cCircle", {"start": v(-623.6, 136.5) * mm, "mid": v(-617.24, 151.87) * mm, "end": v(-632.6, 145.5) * mm});
            skPoint(sketch, "E469.cCircle.centerSnap0", {"position": v(-623.6, 128.5) * mm});
            skPoint(sketch, "E469.cCircle.centerSnap1", {"position": v(-640.6, 145.5) * mm});
            skLineSegment(sketch, "E469.0", {"start": v(-623.6, 136.5) * mm, "end": v(-632.6, 136.5) * mm});
            skLineSegment(sketch, "E469.1", {"start": v(-632.6, 136.5) * mm, "end": v(-632.6, 145.5) * mm});
            skPoint(sketch, "E469.0.midPoint", {"position": v(-623.6, 136.5) * mm});
            skArc(sketch, "E470.cCircle", {"start": v(-632.6, 41.5) * mm, "mid": v(-617.24, 35.14) * mm, "end": v(-623.6, 50.5) * mm});
            skPoint(sketch, "E470.cCircle.centerSnap0", {"position": v(-623.6, 58.5) * mm});
            skPoint(sketch, "E470.cCircle.centerSnap1", {"position": v(-640.6, 41.5) * mm});
            skLineSegment(sketch, "E470.0", {"start": v(-632.6, 50.5) * mm, "end": v(-623.6, 50.5) * mm});
            skLineSegment(sketch, "E470.3", {"start": v(-632.6, 41.5) * mm, "end": v(-632.6, 50.5) * mm});
            skPoint(sketch, "E470.0.midPoint", {"position": v(-623.6, 50.5) * mm});
            skPoint(sketch, "E471.orphan", {"position": v(-1115.68, 146) * mm});
            skPoint(sketch, "E472.orphan", {"position": v(-1097.68, 164) * mm});
            skPoint(sketch, "E473.orphan", {"position": v(-1115.68, 60) * mm});
            skPoint(sketch, "E474.orphan", {"position": v(-861.68, 42) * mm});
            skPoint(sketch, "E475.orphan", {"position": v(-843.68, 60) * mm});
            skPoint(sketch, "E476.orphan", {"position": v(-843.68, 146) * mm});
            skPoint(sketch, "E477.orphan", {"position": v(-736.6, 136.5) * mm});
            skPoint(sketch, "E478.orphan", {"position": v(-718.6, 154.5) * mm});
            skPoint(sketch, "E479.orphan", {"position": v(-736.6, 50.5) * mm});
            skPoint(sketch, "E480.orphan", {"position": v(-632.6, 32.5) * mm});
            skPoint(sketch, "E481.orphan", {"position": v(-614.6, 50.5) * mm});
            skPoint(sketch, "E482.orphan", {"position": v(-614.6, 136.5) * mm});
            skArc(sketch, "E483.cCircle", {"start": v(-514.05, 147.99) * mm, "mid": v(-529.41, 154.35) * mm, "end": v(-523.05, 138.99) * mm});
            skPoint(sketch, "E483.cCircle.centerSnap0", {"position": v(-506.14, 147.99) * mm});
            skPoint(sketch, "E483.cCircle.centerSnap1", {"position": v(-523.05, 130.99) * mm});
            skLineSegment(sketch, "E483.0", {"start": v(-514.05, 138.99) * mm, "end": v(-523.05, 138.99) * mm});
            skLineSegment(sketch, "E483.3", {"start": v(-514.05, 147.99) * mm, "end": v(-514.05, 138.99) * mm});
            skPoint(sketch, "E483.0.midPoint", {"position": v(-523.05, 138.99) * mm});
            skArc(sketch, "E484.cCircle", {"start": v(-523.05, 52.99) * mm, "mid": v(-529.41, 37.63) * mm, "end": v(-514.05, 43.99) * mm});
            skPoint(sketch, "E484.cCircle.centerSnap0", {"position": v(-506.14, 43.99) * mm});
            skPoint(sketch, "E484.cCircle.centerSnap1", {"position": v(-523.05, 60.99) * mm});
            skLineSegment(sketch, "E484.0", {"start": v(-523.05, 52.99) * mm, "end": v(-514.05, 52.99) * mm});
            skLineSegment(sketch, "E484.1", {"start": v(-514.05, 52.99) * mm, "end": v(-514.05, 43.99) * mm});
            skPoint(sketch, "E484.0.midPoint", {"position": v(-523.05, 52.99) * mm});
            skArc(sketch, "E485.cCircle", {"start": v(-127.85, 43.99) * mm, "mid": v(-112.48, 37.63) * mm, "end": v(-118.85, 52.99) * mm});
            skPoint(sketch, "E485.cCircle.centerSnap0", {"position": v(-118.85, 60.99) * mm});
            skPoint(sketch, "E485.cCircle.centerSnap1", {"position": v(-135.75, 43.99) * mm});
            skLineSegment(sketch, "E485.0", {"start": v(-127.85, 52.99) * mm, "end": v(-118.85, 52.99) * mm});
            skLineSegment(sketch, "E485.3", {"start": v(-127.85, 43.99) * mm, "end": v(-127.85, 52.99) * mm});
            skPoint(sketch, "E485.0.midPoint", {"position": v(-118.85, 52.99) * mm});
            skArc(sketch, "E486.cCircle", {"start": v(-118.85, 138.99) * mm, "mid": v(-112.48, 154.35) * mm, "end": v(-127.85, 147.99) * mm});
            skPoint(sketch, "E486.cCircle.centerSnap0", {"position": v(-118.85, 130.99) * mm});
            skPoint(sketch, "E486.cCircle.centerSnap1", {"position": v(-135.75, 147.99) * mm});
            skLineSegment(sketch, "E486.0", {"start": v(-118.85, 138.99) * mm, "end": v(-127.85, 138.99) * mm});
            skLineSegment(sketch, "E486.1", {"start": v(-127.85, 138.99) * mm, "end": v(-127.85, 147.99) * mm});
            skPoint(sketch, "E486.0.midPoint", {"position": v(-118.85, 138.99) * mm});
            skPoint(sketch, "E487.orphan", {"position": v(-514.05, 156.99) * mm});
            skPoint(sketch, "E488.orphan", {"position": v(-532.05, 138.99) * mm});
            skPoint(sketch, "E489.orphan", {"position": v(-532.05, 52.99) * mm});
            skPoint(sketch, "E490.orphan", {"position": v(-127.85, 34.99) * mm});
            skPoint(sketch, "E491.orphan", {"position": v(-109.85, 52.99) * mm});
            skPoint(sketch, "E492.orphan", {"position": v(-109.85, 138.99) * mm});
            skLineSegment(sketch, "E493", {"start": v(-540.95, 25.99) * mm, "end": v(-100.95, 25.99) * mm});
            skArc(sketch, "E494.cCircle", {"start": v(2.1, 141.72) * mm, "mid": v(8.47, 157.09) * mm, "end": v(-6.9, 150.72) * mm});
            skPoint(sketch, "E494.cCircle.centerSnap0", {"position": v(2.1, 133.72) * mm});
            skPoint(sketch, "E494.cCircle.centerSnap1", {"position": v(-14.9, 150.72) * mm});
            skLineSegment(sketch, "E494.0", {"start": v(2.1, 141.72) * mm, "end": v(-6.9, 141.72) * mm});
            skLineSegment(sketch, "E494.1", {"start": v(-6.9, 141.72) * mm, "end": v(-6.9, 150.72) * mm});
            skPoint(sketch, "E494.0.midPoint", {"position": v(2.1, 141.72) * mm});
            skArc(sketch, "E495.cCircle", {"start": v(-6.9, 46.72) * mm, "mid": v(8.47, 40.36) * mm, "end": v(2.1, 55.72) * mm});
            skPoint(sketch, "E495.cCircle.centerSnap0", {"position": v(2.1, 63.72) * mm});
            skPoint(sketch, "E495.cCircle.centerSnap1", {"position": v(-14.9, 46.72) * mm});
            skLineSegment(sketch, "E495.0", {"start": v(-6.9, 55.72) * mm, "end": v(2.1, 55.72) * mm});
            skLineSegment(sketch, "E495.3", {"start": v(-6.9, 46.72) * mm, "end": v(-6.9, 55.72) * mm});
            skPoint(sketch, "E495.0.midPoint", {"position": v(2.1, 55.72) * mm});
            skArc(sketch, "E496.cCircle", {"start": v(195.75, 141) * mm, "mid": v(202.11, 156.36) * mm, "end": v(186.75, 150) * mm});
            skPoint(sketch, "E496.cCircle.centerSnap0", {"position": v(195.75, 133) * mm});
            skPoint(sketch, "E496.cCircle.centerSnap1", {"position": v(178.75, 150) * mm});
            skLineSegment(sketch, "E496.0", {"start": v(195.75, 141) * mm, "end": v(186.75, 141) * mm});
            skLineSegment(sketch, "E496.1", {"start": v(186.75, 141) * mm, "end": v(186.75, 150) * mm});
            skPoint(sketch, "E496.0.midPoint", {"position": v(195.75, 141) * mm});
            skArc(sketch, "E497.cCircle", {"start": v(186.75, 46) * mm, "mid": v(202.11, 39.63) * mm, "end": v(195.75, 55) * mm});
            skPoint(sketch, "E497.cCircle.centerSnap0", {"position": v(195.75, 63) * mm});
            skPoint(sketch, "E497.cCircle.centerSnap1", {"position": v(178.75, 46) * mm});
            skLineSegment(sketch, "E497.0", {"start": v(186.75, 55) * mm, "end": v(195.75, 55) * mm});
            skLineSegment(sketch, "E497.3", {"start": v(186.75, 46) * mm, "end": v(186.75, 55) * mm});
            skPoint(sketch, "E497.0.midPoint", {"position": v(195.75, 55) * mm});
            skPoint(sketch, "E498.orphan", {"position": v(11.1, 141.72) * mm});
            skPoint(sketch, "E499.orphan", {"position": v(-6.9, 37.72) * mm});
            skPoint(sketch, "E500.orphan", {"position": v(11.1, 55.72) * mm});
            skPoint(sketch, "E501.orphan", {"position": v(204.75, 141) * mm});
            skPoint(sketch, "E502.orphan", {"position": v(204.75, 55) * mm});
            skPoint(sketch, "E503.orphan", {"position": v(186.75, 37) * mm});
            skArc(sketch, "E504.cCircle", {"start": v(337.8, 146.82) * mm, "mid": v(322.43, 153.18) * mm, "end": v(328.8, 137.82) * mm});
            skPoint(sketch, "E504.cCircle.centerSnap0", {"position": v(345.8, 146.82) * mm});
            skPoint(sketch, "E504.cCircle.centerSnap1", {"position": v(328.8, 129.82) * mm});
            skLineSegment(sketch, "E504.0", {"start": v(337.8, 137.82) * mm, "end": v(328.8, 137.82) * mm});
            skLineSegment(sketch, "E504.3", {"start": v(337.8, 146.82) * mm, "end": v(337.8, 137.82) * mm});
            skPoint(sketch, "E504.0.midPoint", {"position": v(328.8, 137.82) * mm});
            skArc(sketch, "E505.cCircle", {"start": v(328.8, 51.82) * mm, "mid": v(322.43, 36.45) * mm, "end": v(337.8, 42.82) * mm});
            skPoint(sketch, "E505.cCircle.centerSnap0", {"position": v(328.8, 59.82) * mm});
            skPoint(sketch, "E505.cCircle.centerSnap1", {"position": v(345.8, 42.82) * mm});
            skLineSegment(sketch, "E505.0", {"start": v(328.8, 51.82) * mm, "end": v(337.8, 51.82) * mm});
            skLineSegment(sketch, "E505.1", {"start": v(337.8, 51.82) * mm, "end": v(337.8, 42.82) * mm});
            skPoint(sketch, "E505.0.midPoint", {"position": v(328.8, 51.82) * mm});
            skArc(sketch, "E506.cCircle", {"start": v(473.8, 42.82) * mm, "mid": v(489.16, 36.45) * mm, "end": v(482.8, 51.82) * mm});
            skPoint(sketch, "E506.cCircle.centerSnap0", {"position": v(482.8, 59.82) * mm});
            skPoint(sketch, "E506.cCircle.centerSnap1", {"position": v(465.8, 42.82) * mm});
            skLineSegment(sketch, "E506.0", {"start": v(473.8, 51.82) * mm, "end": v(482.8, 51.82) * mm});
            skLineSegment(sketch, "E506.3", {"start": v(473.8, 42.82) * mm, "end": v(473.8, 51.82) * mm});
            skPoint(sketch, "E506.0.midPoint", {"position": v(482.8, 51.82) * mm});
            skArc(sketch, "E507.cCircle", {"start": v(482.8, 137.82) * mm, "mid": v(489.16, 153.18) * mm, "end": v(473.8, 146.82) * mm});
            skPoint(sketch, "E507.cCircle.centerSnap0", {"position": v(482.8, 129.82) * mm});
            skPoint(sketch, "E507.cCircle.centerSnap1", {"position": v(465.8, 146.82) * mm});
            skLineSegment(sketch, "E507.0", {"start": v(482.8, 137.82) * mm, "end": v(473.8, 137.82) * mm});
            skLineSegment(sketch, "E507.1", {"start": v(473.8, 137.82) * mm, "end": v(473.8, 146.82) * mm});
            skPoint(sketch, "E507.0.midPoint", {"position": v(482.8, 137.82) * mm});
            skPoint(sketch, "E508.orphan", {"position": v(337.8, 155.82) * mm});
            skPoint(sketch, "E509.orphan", {"position": v(319.8, 137.82) * mm});
            skPoint(sketch, "E510.orphan", {"position": v(319.8, 51.82) * mm});
            skPoint(sketch, "E511.orphan", {"position": v(491.8, 137.82) * mm});
            skPoint(sketch, "E512.orphan", {"position": v(491.8, 51.82) * mm});
            skPoint(sketch, "E513.orphan", {"position": v(473.8, 33.82) * mm});
            skArc(sketch, "E514.cCircle", {"start": v(606.39, 153.67) * mm, "mid": v(591.02, 160.04) * mm, "end": v(597.39, 144.67) * mm});
            skPoint(sketch, "E514.cCircle.centerSnap0", {"position": v(614.39, 153.67) * mm});
            skPoint(sketch, "E514.cCircle.centerSnap1", {"position": v(597.39, 136.67) * mm});
            skLineSegment(sketch, "E514.0", {"start": v(606.39, 144.67) * mm, "end": v(597.39, 144.67) * mm});
            skLineSegment(sketch, "E514.3", {"start": v(606.39, 153.67) * mm, "end": v(606.39, 144.67) * mm});
            skPoint(sketch, "E514.0.midPoint", {"position": v(597.39, 144.67) * mm});
            skArc(sketch, "E515.cCircle", {"start": v(597.39, 58.67) * mm, "mid": v(591.02, 43.3) * mm, "end": v(606.39, 49.67) * mm});
            skPoint(sketch, "E515.cCircle.centerSnap0", {"position": v(597.39, 66.67) * mm});
            skPoint(sketch, "E515.cCircle.centerSnap1", {"position": v(614.39, 49.67) * mm});
            skLineSegment(sketch, "E515.0", {"start": v(597.39, 58.67) * mm, "end": v(606.39, 58.67) * mm});
            skLineSegment(sketch, "E515.1", {"start": v(606.39, 58.67) * mm, "end": v(606.39, 49.67) * mm});
            skPoint(sketch, "E515.0.midPoint", {"position": v(597.39, 58.67) * mm});
            skArc(sketch, "E516.cCircle", {"start": v(762.39, 49.67) * mm, "mid": v(777.75, 43.3) * mm, "end": v(771.39, 58.67) * mm});
            skPoint(sketch, "E516.cCircle.centerSnap0", {"position": v(771.39, 66.67) * mm});
            skPoint(sketch, "E516.cCircle.centerSnap1", {"position": v(754.39, 49.67) * mm});
            skLineSegment(sketch, "E516.0", {"start": v(762.39, 58.67) * mm, "end": v(771.39, 58.67) * mm});
            skLineSegment(sketch, "E516.3", {"start": v(762.39, 49.67) * mm, "end": v(762.39, 58.67) * mm});
            skPoint(sketch, "E516.0.midPoint", {"position": v(771.39, 58.67) * mm});
            skArc(sketch, "E517.cCircle", {"start": v(771.39, 144.67) * mm, "mid": v(777.75, 160.04) * mm, "end": v(762.39, 153.67) * mm});
            skPoint(sketch, "E517.cCircle.centerSnap0", {"position": v(771.39, 136.67) * mm});
            skPoint(sketch, "E517.cCircle.centerSnap1", {"position": v(754.39, 153.67) * mm});
            skLineSegment(sketch, "E517.0", {"start": v(771.39, 144.67) * mm, "end": v(762.39, 144.67) * mm});
            skLineSegment(sketch, "E517.1", {"start": v(762.39, 144.67) * mm, "end": v(762.39, 153.67) * mm});
            skPoint(sketch, "E517.0.midPoint", {"position": v(771.39, 144.67) * mm});
            skPoint(sketch, "E518.orphan", {"position": v(588.39, 144.67) * mm});
            skPoint(sketch, "E519.orphan", {"position": v(606.39, 162.67) * mm});
            skPoint(sketch, "E520.orphan", {"position": v(588.39, 58.67) * mm});
            skPoint(sketch, "E521.orphan", {"position": v(780.39, 58.67) * mm});
            skPoint(sketch, "E522.orphan", {"position": v(762.39, 40.67) * mm});
            skPoint(sketch, "E523.orphan", {"position": v(780.39, 144.67) * mm});
            skArc(sketch, "E524.cCircle", {"start": v(879.51, 148.38) * mm, "mid": v(864.15, 154.75) * mm, "end": v(870.51, 139.38) * mm});
            skPoint(sketch, "E524.cCircle.centerSnap0", {"position": v(887.51, 148.38) * mm});
            skPoint(sketch, "E524.cCircle.centerSnap1", {"position": v(870.51, 131.38) * mm});
            skLineSegment(sketch, "E524.0", {"start": v(879.51, 139.38) * mm, "end": v(870.51, 139.38) * mm});
            skLineSegment(sketch, "E524.3", {"start": v(879.51, 148.38) * mm, "end": v(879.51, 139.38) * mm});
            skPoint(sketch, "E524.0.midPoint", {"position": v(870.51, 139.38) * mm});
            skArc(sketch, "E525.cCircle", {"start": v(870.51, 53.38) * mm, "mid": v(864.15, 38.02) * mm, "end": v(879.51, 44.38) * mm});
            skPoint(sketch, "E525.cCircle.centerSnap0", {"position": v(887.51, 44.38) * mm});
            skPoint(sketch, "E525.cCircle.centerSnap1", {"position": v(870.51, 61.38) * mm});
            skLineSegment(sketch, "E525.0", {"start": v(870.51, 53.38) * mm, "end": v(879.51, 53.38) * mm});
            skLineSegment(sketch, "E525.1", {"start": v(879.51, 53.38) * mm, "end": v(879.51, 44.38) * mm});
            skPoint(sketch, "E525.0.midPoint", {"position": v(870.51, 53.38) * mm});
            skArc(sketch, "E526.cCircle", {"start": v(1065.51, 44.38) * mm, "mid": v(1080.88, 38.02) * mm, "end": v(1074.51, 53.38) * mm});
            skPoint(sketch, "E526.cCircle.centerSnap0", {"position": v(1074.51, 61.38) * mm});
            skPoint(sketch, "E526.cCircle.centerSnap1", {"position": v(1057.51, 44.38) * mm});
            skLineSegment(sketch, "E526.0", {"start": v(1065.51, 53.38) * mm, "end": v(1074.51, 53.38) * mm});
            skLineSegment(sketch, "E526.3", {"start": v(1065.51, 44.38) * mm, "end": v(1065.51, 53.38) * mm});
            skPoint(sketch, "E526.0.midPoint", {"position": v(1074.51, 53.38) * mm});
            skArc(sketch, "E527.cCircle", {"start": v(1074.51, 139.38) * mm, "mid": v(1080.88, 154.75) * mm, "end": v(1065.51, 148.38) * mm});
            skPoint(sketch, "E527.cCircle.centerSnap0", {"position": v(1074.51, 131.38) * mm});
            skPoint(sketch, "E527.cCircle.centerSnap1", {"position": v(1057.51, 148.38) * mm});
            skLineSegment(sketch, "E527.0", {"start": v(1074.51, 139.38) * mm, "end": v(1065.51, 139.38) * mm});
            skLineSegment(sketch, "E527.1", {"start": v(1065.51, 139.38) * mm, "end": v(1065.51, 148.38) * mm});
            skPoint(sketch, "E527.0.midPoint", {"position": v(1074.51, 139.38) * mm});
            skPoint(sketch, "E528.orphan", {"position": v(861.51, 139.38) * mm});
            skPoint(sketch, "E529.orphan", {"position": v(861.51, 53.38) * mm});
            skPoint(sketch, "E530.orphan", {"position": v(879.51, 157.38) * mm});
            skPoint(sketch, "E531.orphan", {"position": v(1083.51, 139.38) * mm});
            skPoint(sketch, "E532.orphan", {"position": v(1065.51, 35.38) * mm});
            skPoint(sketch, "E533.orphan", {"position": v(1083.51, 53.38) * mm});
            skSolve(sketch);
        }
        {
            var Q0;
            Q0 = qSketchRegion(id + "F0", true);
            extrude(context, id + "F1", {"entities" : qUnion([Q0]), "depth" : 190 * mm});
        }
        {
            var Q0;
            Q0=qCreatedBy(makeId("Top.planeOp"),FACE);
            var sketch = newSketch(context, id + "F2", { "sketchPlane" : qUnion([Q0])});
            skLineSegment(sketch, "E534", {"start": v(-355.18, -76.24) * mm, "end": v(-355.18, -216.24) * mm});
            skLineSegment(sketch, "E535", {"start": v(-355.18, -216.24) * mm, "end": v(-65.18, -216.24) * mm});
            skLineSegment(sketch, "E536", {"start": v(-65.18, -216.24) * mm, "end": v(-65.18, -76.24) * mm});
            skLineSegment(sketch, "E537", {"start": v(-65.18, -76.24) * mm, "end": v(-355.18, -76.24) * mm});
            skLineSegment(sketch, "E538", {"start": v(-320.18, -85.24) * mm, "end": v(-320.18, -103.24) * mm});
            skLineSegment(sketch, "E539", {"start": v(-320.18, -103.24) * mm, "end": v(-290.43, -103.24) * mm});
            skLineSegment(sketch, "E540", {"start": v(-290.43, -103.24) * mm, "end": v(-290.43, -85.24) * mm});
            skLineSegment(sketch, "E541", {"start": v(-290.43, -85.24) * mm, "end": v(-320.18, -85.24) * mm});
            skLineSegment(sketch, "E542", {"start": v(-282.43, -85.24) * mm, "end": v(-282.43, -103.24) * mm});
            skLineSegment(sketch, "E543", {"start": v(-282.43, -103.24) * mm, "end": v(-252.68, -103.24) * mm});
            skLineSegment(sketch, "E544", {"start": v(-252.68, -103.24) * mm, "end": v(-252.68, -85.24) * mm});
            skLineSegment(sketch, "E545", {"start": v(-252.68, -85.24) * mm, "end": v(-282.43, -85.24) * mm});
            skLineSegment(sketch, "E546", {"start": v(-244.68, -85.24) * mm, "end": v(-244.68, -120.24) * mm});
            skLineSegment(sketch, "E547", {"start": v(-244.68, -120.24) * mm, "end": v(-214.18, -120.24) * mm});
            skLineSegment(sketch, "E548", {"start": v(-214.18, -120.24) * mm, "end": v(-214.18, -85.24) * mm});
            skLineSegment(sketch, "E549", {"start": v(-214.18, -85.24) * mm, "end": v(-244.68, -85.24) * mm});
            skLineSegment(sketch, "E550", {"start": v(-206.18, -85.24) * mm, "end": v(-206.18, -120.24) * mm});
            skLineSegment(sketch, "E551", {"start": v(-206.18, -120.24) * mm, "end": v(-175.68, -120.24) * mm});
            skLineSegment(sketch, "E552", {"start": v(-175.68, -120.24) * mm, "end": v(-175.68, -85.24) * mm});
            skLineSegment(sketch, "E553", {"start": v(-175.68, -85.24) * mm, "end": v(-206.18, -85.24) * mm});
            skLineSegment(sketch, "E554", {"start": v(-167.68, -85.24) * mm, "end": v(-167.68, -103.24) * mm});
            skLineSegment(sketch, "E555", {"start": v(-167.68, -103.24) * mm, "end": v(-137.93, -103.24) * mm});
            skLineSegment(sketch, "E556", {"start": v(-137.93, -103.24) * mm, "end": v(-137.93, -85.24) * mm});
            skLineSegment(sketch, "E557", {"start": v(-137.93, -85.24) * mm, "end": v(-167.68, -85.24) * mm});
            skLineSegment(sketch, "E558", {"start": v(-129.93, -85.24) * mm, "end": v(-129.93, -103.24) * mm});
            skLineSegment(sketch, "E559", {"start": v(-129.93, -103.24) * mm, "end": v(-100.18, -103.24) * mm});
            skLineSegment(sketch, "E560", {"start": v(-100.18, -103.24) * mm, "end": v(-100.18, -85.24) * mm});
            skLineSegment(sketch, "E561", {"start": v(-100.18, -85.24) * mm, "end": v(-129.93, -85.24) * mm});
            skLineSegment(sketch, "E562", {"start": v(-92.18, -111.24) * mm, "end": v(-92.18, -142.24) * mm});
            skLineSegment(sketch, "E563", {"start": v(-92.18, -142.24) * mm, "end": v(-74.18, -142.24) * mm});
            skLineSegment(sketch, "E564", {"start": v(-74.18, -142.24) * mm, "end": v(-74.18, -111.24) * mm});
            skLineSegment(sketch, "E565", {"start": v(-74.18, -111.24) * mm, "end": v(-92.18, -111.24) * mm});
            skLineSegment(sketch, "E566", {"start": v(-320.18, -111.24) * mm, "end": v(-320.18, -181.24) * mm});
            skLineSegment(sketch, "E567", {"start": v(-320.18, -181.24) * mm, "end": v(-252.68, -181.24) * mm});
            skLineSegment(sketch, "E568", {"start": v(-252.68, -181.24) * mm, "end": v(-252.68, -111.24) * mm});
            skLineSegment(sketch, "E569", {"start": v(-252.68, -111.24) * mm, "end": v(-320.18, -111.24) * mm});
            skLineSegment(sketch, "E570", {"start": v(-346.18, -111.24) * mm, "end": v(-346.18, -142.24) * mm});
            skLineSegment(sketch, "E571", {"start": v(-346.18, -142.24) * mm, "end": v(-328.18, -142.24) * mm});
            skLineSegment(sketch, "E572", {"start": v(-328.18, -142.24) * mm, "end": v(-328.18, -111.24) * mm});
            skLineSegment(sketch, "E573", {"start": v(-328.18, -111.24) * mm, "end": v(-346.18, -111.24) * mm});
            skLineSegment(sketch, "E574", {"start": v(-346.18, -150.24) * mm, "end": v(-346.18, -181.24) * mm});
            skLineSegment(sketch, "E575", {"start": v(-346.18, -181.24) * mm, "end": v(-328.18, -181.24) * mm});
            skLineSegment(sketch, "E576", {"start": v(-328.18, -181.24) * mm, "end": v(-328.18, -150.24) * mm});
            skLineSegment(sketch, "E577", {"start": v(-328.18, -150.24) * mm, "end": v(-346.18, -150.24) * mm});
            skLineSegment(sketch, "E578", {"start": v(-320.18, -189.24) * mm, "end": v(-320.18, -207.24) * mm});
            skLineSegment(sketch, "E579", {"start": v(-320.18, -207.24) * mm, "end": v(-290.43, -207.24) * mm});
            skLineSegment(sketch, "E580", {"start": v(-290.43, -207.24) * mm, "end": v(-290.43, -189.24) * mm});
            skLineSegment(sketch, "E581", {"start": v(-290.43, -189.24) * mm, "end": v(-320.18, -189.24) * mm});
            skLineSegment(sketch, "E582", {"start": v(-282.43, -189.24) * mm, "end": v(-282.43, -207.24) * mm});
            skLineSegment(sketch, "E583", {"start": v(-282.43, -207.24) * mm, "end": v(-252.68, -207.24) * mm});
            skLineSegment(sketch, "E584", {"start": v(-252.68, -207.24) * mm, "end": v(-252.68, -189.24) * mm});
            skLineSegment(sketch, "E585", {"start": v(-252.68, -189.24) * mm, "end": v(-282.43, -189.24) * mm});
            skLineSegment(sketch, "E586", {"start": v(-244.68, -128.24) * mm, "end": v(-244.68, -164.24) * mm});
            skLineSegment(sketch, "E587", {"start": v(-244.68, -164.24) * mm, "end": v(-175.68, -164.24) * mm});
            skLineSegment(sketch, "E588", {"start": v(-175.68, -164.24) * mm, "end": v(-175.68, -128.24) * mm});
            skLineSegment(sketch, "E589", {"start": v(-175.68, -128.24) * mm, "end": v(-244.68, -128.24) * mm});
            skLineSegment(sketch, "E590", {"start": v(-244.68, -172.24) * mm, "end": v(-244.68, -207.24) * mm});
            skLineSegment(sketch, "E591", {"start": v(-244.68, -207.24) * mm, "end": v(-214.18, -207.24) * mm});
            skLineSegment(sketch, "E592", {"start": v(-214.18, -207.24) * mm, "end": v(-214.18, -172.24) * mm});
            skLineSegment(sketch, "E593", {"start": v(-214.18, -172.24) * mm, "end": v(-244.68, -172.24) * mm});
            skLineSegment(sketch, "E594", {"start": v(-206.18, -172.24) * mm, "end": v(-206.18, -207.24) * mm});
            skLineSegment(sketch, "E595", {"start": v(-206.18, -207.24) * mm, "end": v(-175.68, -207.24) * mm});
            skLineSegment(sketch, "E596", {"start": v(-175.68, -207.24) * mm, "end": v(-175.68, -172.24) * mm});
            skLineSegment(sketch, "E597", {"start": v(-175.68, -172.24) * mm, "end": v(-206.18, -172.24) * mm});
            skLineSegment(sketch, "E598", {"start": v(-167.68, -111.24) * mm, "end": v(-167.68, -181.24) * mm});
            skLineSegment(sketch, "E599", {"start": v(-167.68, -181.24) * mm, "end": v(-100.18, -181.24) * mm});
            skLineSegment(sketch, "E600", {"start": v(-100.18, -181.24) * mm, "end": v(-100.18, -111.24) * mm});
            skLineSegment(sketch, "E601", {"start": v(-100.18, -111.24) * mm, "end": v(-167.68, -111.24) * mm});
            skLineSegment(sketch, "E602", {"start": v(-167.68, -189.24) * mm, "end": v(-167.68, -207.24) * mm});
            skLineSegment(sketch, "E603", {"start": v(-167.68, -207.24) * mm, "end": v(-137.93, -207.24) * mm});
            skLineSegment(sketch, "E604", {"start": v(-137.93, -207.24) * mm, "end": v(-137.93, -189.24) * mm});
            skLineSegment(sketch, "E605", {"start": v(-137.93, -189.24) * mm, "end": v(-167.68, -189.24) * mm});
            skLineSegment(sketch, "E606", {"start": v(-129.93, -189.24) * mm, "end": v(-129.93, -207.24) * mm});
            skLineSegment(sketch, "E607", {"start": v(-129.93, -207.24) * mm, "end": v(-100.18, -207.24) * mm});
            skLineSegment(sketch, "E608", {"start": v(-100.18, -207.24) * mm, "end": v(-100.18, -189.24) * mm});
            skLineSegment(sketch, "E609", {"start": v(-100.18, -189.24) * mm, "end": v(-129.93, -189.24) * mm});
            skLineSegment(sketch, "E610", {"start": v(-92.18, -150.24) * mm, "end": v(-92.18, -181.24) * mm});
            skLineSegment(sketch, "E611", {"start": v(-92.18, -181.24) * mm, "end": v(-74.18, -181.24) * mm});
            skLineSegment(sketch, "E612", {"start": v(-74.18, -181.24) * mm, "end": v(-74.18, -150.24) * mm});
            skLineSegment(sketch, "E613", {"start": v(-74.18, -150.24) * mm, "end": v(-92.18, -150.24) * mm});
            skArc(sketch, "E614.cCircle", {"start": v(-328.18, -94.24) * mm, "mid": v(-343.55, -87.88) * mm, "end": v(-337.18, -103.24) * mm});
            skPoint(sketch, "E614.cCircle.centerSnap0", {"position": v(-337.18, -111.24) * mm});
            skPoint(sketch, "E614.cCircle.centerSnap1", {"position": v(-320.18, -94.24) * mm});
            skLineSegment(sketch, "E614.0", {"start": v(-328.18, -103.24) * mm, "end": v(-337.18, -103.24) * mm});
            skLineSegment(sketch, "E614.3", {"start": v(-328.18, -94.24) * mm, "end": v(-328.18, -103.24) * mm});
            skPoint(sketch, "E614.0.midPoint", {"position": v(-337.18, -103.24) * mm});
            skArc(sketch, "E615.cCircle", {"start": v(-337.18, -189.24) * mm, "mid": v(-343.55, -204.6) * mm, "end": v(-328.18, -198.24) * mm});
            skPoint(sketch, "E615.cCircle.centerSnap0", {"position": v(-337.18, -181.24) * mm});
            skPoint(sketch, "E615.cCircle.centerSnap1", {"position": v(-320.18, -198.24) * mm});
            skLineSegment(sketch, "E615.0", {"start": v(-337.18, -189.24) * mm, "end": v(-328.18, -189.24) * mm});
            skLineSegment(sketch, "E615.1", {"start": v(-328.18, -189.24) * mm, "end": v(-328.18, -198.24) * mm});
            skPoint(sketch, "E615.0.midPoint", {"position": v(-337.18, -189.24) * mm});
            skPoint(sketch, "E616.orphan", {"position": v(-346.18, -103.24) * mm});
            skPoint(sketch, "E617.orphan", {"position": v(-328.18, -85.24) * mm});
            skPoint(sketch, "E618.orphan", {"position": v(-346.18, -189.24) * mm});
            skArc(sketch, "E619.cCircle", {"start": v(-83.18, -103.24) * mm, "mid": v(-76.82, -87.88) * mm, "end": v(-92.18, -94.24) * mm});
            skPoint(sketch, "E619.cCircle.centerSnap0", {"position": v(-83.18, -111.24) * mm});
            skPoint(sketch, "E619.cCircle.centerSnap1", {"position": v(-100.18, -94.24) * mm});
            skLineSegment(sketch, "E619.0", {"start": v(-83.18, -103.24) * mm, "end": v(-92.18, -103.24) * mm});
            skLineSegment(sketch, "E619.1", {"start": v(-92.18, -103.24) * mm, "end": v(-92.18, -94.24) * mm});
            skPoint(sketch, "E619.0.midPoint", {"position": v(-83.18, -103.24) * mm});
            skArc(sketch, "E620.cCircle", {"start": v(-92.18, -198.24) * mm, "mid": v(-76.82, -204.6) * mm, "end": v(-83.18, -189.24) * mm});
            skPoint(sketch, "E620.cCircle.centerSnap0", {"position": v(-83.18, -181.24) * mm});
            skPoint(sketch, "E620.cCircle.centerSnap1", {"position": v(-100.18, -198.24) * mm});
            skLineSegment(sketch, "E620.0", {"start": v(-92.18, -189.24) * mm, "end": v(-83.18, -189.24) * mm});
            skLineSegment(sketch, "E620.3", {"start": v(-92.18, -198.24) * mm, "end": v(-92.18, -189.24) * mm});
            skPoint(sketch, "E620.0.midPoint", {"position": v(-83.18, -189.24) * mm});
            skPoint(sketch, "E621.orphan", {"position": v(-74.18, -103.24) * mm});
            skPoint(sketch, "E622.orphan", {"position": v(-92.18, -207.24) * mm});
            skPoint(sketch, "E623.orphan", {"position": v(-74.18, -189.24) * mm});
            skSolve(sketch);
        }
        {
            var Q0;
            Q0 = qSketchRegion(id + "F2", true);
            extrude(context, id + "F3", {"entities" : qUnion([Q0]), "depth" : 90 * mm});
        }
        {
            var Q0;
            Q0=makeQuery(id+"F1.opExtrude","SWEPT_BODY",BODY,{"disambiguationData":[OSD([sQuery(id+"F0.wireOp",EDGE,"E0"),sQuery(id+"F0.wireOp",EDGE,"E1"),sQuery(id+"F0.wireOp",EDGE,"E2"),sQuery(id+"F0.wireOp",EDGE,"E3"),sQuery(id+"F0.wireOp",EDGE,"E4"),sQuery(id+"F0.wireOp",EDGE,"E5"),sQuery(id+"F0.wireOp",EDGE,"E6"),sQuery(id+"F0.wireOp",EDGE,"E7"),sQuery(id+"F0.wireOp",EDGE,"E8"),sQuery(id+"F0.wireOp",EDGE,"E9"),sQuery(id+"F0.wireOp",EDGE,"E10"),sQuery(id+"F0.wireOp",EDGE,"E11"),sQuery(id+"F0.wireOp",EDGE,"E12"),sQuery(id+"F0.wireOp",EDGE,"E13"),sQuery(id+"F0.wireOp",EDGE,"E14"),sQuery(id+"F0.wireOp",EDGE,"E15"),sQuery(id+"F0.wireOp",EDGE,"E16"),sQuery(id+"F0.wireOp",EDGE,"E17"),sQuery(id+"F0.wireOp",EDGE,"E18"),sQuery(id+"F0.wireOp",EDGE,"E19"),sQuery(id+"F0.wireOp",EDGE,"E20"),sQuery(id+"F0.wireOp",EDGE,"E21"),sQuery(id+"F0.wireOp",EDGE,"E22"),sQuery(id+"F0.wireOp",EDGE,"E23"),sQuery(id+"F0.wireOp",EDGE,"E24"),sQuery(id+"F0.wireOp",EDGE,"E25"),sQuery(id+"F0.wireOp",EDGE,"E26"),sQuery(id+"F0.wireOp",EDGE,"E27"),sQuery(id+"F0.wireOp",EDGE,"E28"),sQuery(id+"F0.wireOp",EDGE,"E29"),sQuery(id+"F0.wireOp",EDGE,"E30"),sQuery(id+"F0.wireOp",EDGE,"E31"),sQuery(id+"F0.wireOp",EDGE,"E32"),sQuery(id+"F0.wireOp",EDGE,"E33"),sQuery(id+"F0.wireOp",EDGE,"E34"),sQuery(id+"F0.wireOp",EDGE,"E35"),sQuery(id+"F0.wireOp",EDGE,"E36"),sQuery(id+"F0.wireOp",EDGE,"E37"),sQuery(id+"F0.wireOp",EDGE,"E38"),sQuery(id+"F0.wireOp",EDGE,"E39"),sQuery(id+"F0.wireOp",EDGE,"E40"),sQuery(id+"F0.wireOp",EDGE,"E41"),sQuery(id+"F0.wireOp",EDGE,"E42"),sQuery(id+"F0.wireOp",EDGE,"E43"),sQuery(id+"F0.wireOp",EDGE,"E44"),sQuery(id+"F0.wireOp",EDGE,"E45"),sQuery(id+"F0.wireOp",EDGE,"E46"),sQuery(id+"F0.wireOp",EDGE,"E47"),sQuery(id+"F0.wireOp",EDGE,"E48"),sQuery(id+"F0.wireOp",EDGE,"E49"),sQuery(id+"F0.wireOp",EDGE,"E50"),sQuery(id+"F0.wireOp",EDGE,"E51"),sQuery(id+"F0.wireOp",EDGE,"E52"),sQuery(id+"F0.wireOp",EDGE,"E53"),sQuery(id+"F0.wireOp",EDGE,"E54"),sQuery(id+"F0.wireOp",EDGE,"E55"),sQuery(id+"F0.wireOp",EDGE,"E56"),sQuery(id+"F0.wireOp",EDGE,"E57"),sQuery(id+"F0.wireOp",EDGE,"E58"),sQuery(id+"F0.wireOp",EDGE,"E59"),sQuery(id+"F0.wireOp",EDGE,"E60"),sQuery(id+"F0.wireOp",EDGE,"E61"),sQuery(id+"F0.wireOp",EDGE,"E62"),sQuery(id+"F0.wireOp",EDGE,"E63"),sQuery(id+"F0.wireOp",EDGE,"E64"),sQuery(id+"F0.wireOp",EDGE,"E65"),sQuery(id+"F0.wireOp",EDGE,"E66"),sQuery(id+"F0.wireOp",EDGE,"E67"),sQuery(id+"F0.wireOp",EDGE,"E68"),sQuery(id+"F0.wireOp",EDGE,"E69"),sQuery(id+"F0.wireOp",EDGE,"E70"),sQuery(id+"F0.wireOp",EDGE,"E71"),sQuery(id+"F0.wireOp",EDGE,"E72"),sQuery(id+"F0.wireOp",EDGE,"E73"),sQuery(id+"F0.wireOp",EDGE,"E74"),sQuery(id+"F0.wireOp",EDGE,"E75"),sQuery(id+"F0.wireOp",EDGE,"E76"),sQuery(id+"F0.wireOp",EDGE,"E77"),sQuery(id+"F0.wireOp",EDGE,"E78"),sQuery(id+"F0.wireOp",EDGE,"E79"),sQuery(id+"F0.wireOp",EDGE,"E463.cCircle"),sQuery(id+"F0.wireOp",EDGE,"E463.0"),sQuery(id+"F0.wireOp",EDGE,"E463.3"),sQuery(id+"F0.wireOp",EDGE,"E464.cCircle"),sQuery(id+"F0.wireOp",EDGE,"E464.0"),sQuery(id+"F0.wireOp",EDGE,"E464.1"),sQuery(id+"F0.wireOp",EDGE,"E465.cCircle"),sQuery(id+"F0.wireOp",EDGE,"E465.0"),sQuery(id+"F0.wireOp",EDGE,"E465.3"),sQuery(id+"F0.wireOp",EDGE,"E466.cCircle"),sQuery(id+"F0.wireOp",EDGE,"E466.0"),sQuery(id+"F0.wireOp",EDGE,"E466.1")])]});
            transform(context, id + "F4", {"entities" : qUnion([Q0]), "transformType" : TransformType.TRANSLATION_3D, "dx" : 0 * mm, "dy" : -248 * mm, "dz" : 0 * mm, "makeCopy" : true});
        }
        {
            var Q0;
            Q0=makeQuery(id+"F4.opPattern","COPY",BODY,{"derivedFrom":makeQuery(id+"F1.opExtrude","SWEPT_BODY",BODY,{"disambiguationData":[OSD([sQuery(id+"F0.wireOp",EDGE,"E0"),sQuery(id+"F0.wireOp",EDGE,"E1"),sQuery(id+"F0.wireOp",EDGE,"E2"),sQuery(id+"F0.wireOp",EDGE,"E3"),sQuery(id+"F0.wireOp",EDGE,"E4"),sQuery(id+"F0.wireOp",EDGE,"E5"),sQuery(id+"F0.wireOp",EDGE,"E6"),sQuery(id+"F0.wireOp",EDGE,"E7"),sQuery(id+"F0.wireOp",EDGE,"E8"),sQuery(id+"F0.wireOp",EDGE,"E9"),sQuery(id+"F0.wireOp",EDGE,"E10"),sQuery(id+"F0.wireOp",EDGE,"E11"),sQuery(id+"F0.wireOp",EDGE,"E12"),sQuery(id+"F0.wireOp",EDGE,"E13"),sQuery(id+"F0.wireOp",EDGE,"E14"),sQuery(id+"F0.wireOp",EDGE,"E15"),sQuery(id+"F0.wireOp",EDGE,"E16"),sQuery(id+"F0.wireOp",EDGE,"E17"),sQuery(id+"F0.wireOp",EDGE,"E18"),sQuery(id+"F0.wireOp",EDGE,"E19"),sQuery(id+"F0.wireOp",EDGE,"E20"),sQuery(id+"F0.wireOp",EDGE,"E21"),sQuery(id+"F0.wireOp",EDGE,"E22"),sQuery(id+"F0.wireOp",EDGE,"E23"),sQuery(id+"F0.wireOp",EDGE,"E24"),sQuery(id+"F0.wireOp",EDGE,"E25"),sQuery(id+"F0.wireOp",EDGE,"E26"),sQuery(id+"F0.wireOp",EDGE,"E27"),sQuery(id+"F0.wireOp",EDGE,"E28"),sQuery(id+"F0.wireOp",EDGE,"E29"),sQuery(id+"F0.wireOp",EDGE,"E30"),sQuery(id+"F0.wireOp",EDGE,"E31"),sQuery(id+"F0.wireOp",EDGE,"E32"),sQuery(id+"F0.wireOp",EDGE,"E33"),sQuery(id+"F0.wireOp",EDGE,"E34"),sQuery(id+"F0.wireOp",EDGE,"E35"),sQuery(id+"F0.wireOp",EDGE,"E36"),sQuery(id+"F0.wireOp",EDGE,"E37"),sQuery(id+"F0.wireOp",EDGE,"E38"),sQuery(id+"F0.wireOp",EDGE,"E39"),sQuery(id+"F0.wireOp",EDGE,"E40"),sQuery(id+"F0.wireOp",EDGE,"E41"),sQuery(id+"F0.wireOp",EDGE,"E42"),sQuery(id+"F0.wireOp",EDGE,"E43"),sQuery(id+"F0.wireOp",EDGE,"E44"),sQuery(id+"F0.wireOp",EDGE,"E45"),sQuery(id+"F0.wireOp",EDGE,"E46"),sQuery(id+"F0.wireOp",EDGE,"E47"),sQuery(id+"F0.wireOp",EDGE,"E48"),sQuery(id+"F0.wireOp",EDGE,"E49"),sQuery(id+"F0.wireOp",EDGE,"E50"),sQuery(id+"F0.wireOp",EDGE,"E51"),sQuery(id+"F0.wireOp",EDGE,"E52"),sQuery(id+"F0.wireOp",EDGE,"E53"),sQuery(id+"F0.wireOp",EDGE,"E54"),sQuery(id+"F0.wireOp",EDGE,"E55"),sQuery(id+"F0.wireOp",EDGE,"E56"),sQuery(id+"F0.wireOp",EDGE,"E57"),sQuery(id+"F0.wireOp",EDGE,"E58"),sQuery(id+"F0.wireOp",EDGE,"E59"),sQuery(id+"F0.wireOp",EDGE,"E60"),sQuery(id+"F0.wireOp",EDGE,"E61"),sQuery(id+"F0.wireOp",EDGE,"E62"),sQuery(id+"F0.wireOp",EDGE,"E63"),sQuery(id+"F0.wireOp",EDGE,"E64"),sQuery(id+"F0.wireOp",EDGE,"E65"),sQuery(id+"F0.wireOp",EDGE,"E66"),sQuery(id+"F0.wireOp",EDGE,"E67"),sQuery(id+"F0.wireOp",EDGE,"E68"),sQuery(id+"F0.wireOp",EDGE,"E69"),sQuery(id+"F0.wireOp",EDGE,"E70"),sQuery(id+"F0.wireOp",EDGE,"E71"),sQuery(id+"F0.wireOp",EDGE,"E72"),sQuery(id+"F0.wireOp",EDGE,"E73"),sQuery(id+"F0.wireOp",EDGE,"E74"),sQuery(id+"F0.wireOp",EDGE,"E75"),sQuery(id+"F0.wireOp",EDGE,"E76"),sQuery(id+"F0.wireOp",EDGE,"E77"),sQuery(id+"F0.wireOp",EDGE,"E78"),sQuery(id+"F0.wireOp",EDGE,"E79"),sQuery(id+"F0.wireOp",EDGE,"E463.cCircle"),sQuery(id+"F0.wireOp",EDGE,"E463.0"),sQuery(id+"F0.wireOp",EDGE,"E463.3"),sQuery(id+"F0.wireOp",EDGE,"E464.cCircle"),sQuery(id+"F0.wireOp",EDGE,"E464.0"),sQuery(id+"F0.wireOp",EDGE,"E464.1"),sQuery(id+"F0.wireOp",EDGE,"E465.cCircle"),sQuery(id+"F0.wireOp",EDGE,"E465.0"),sQuery(id+"F0.wireOp",EDGE,"E465.3"),sQuery(id+"F0.wireOp",EDGE,"E466.cCircle"),sQuery(id+"F0.wireOp",EDGE,"E466.0"),sQuery(id+"F0.wireOp",EDGE,"E466.1")])]}),"instanceName":"1"});
            transform(context, id + "F5", {"entities" : qUnion([Q0]), "transformType" : TransformType.TRANSLATION_3D, "dx" : 390 * mm, "dy" : 0 * mm, "dz" : 0 * mm, "makeCopy" : true});
        }
        {
            var Q0;
            Q0=makeQuery(id+"F4.opPattern","COPY",FACE,{"derivedFrom":makeQuery(id+"F1.opExtrude","SWEPT_FACE",FACE,{"disambiguationData":[OSD([sQuery(id+"F0.wireOp",EDGE,"E1")])]}),"instanceName":"1"});
            var sketch = newSketch(context, id + "F6", { "sketchPlane" : qUnion([Q0])});
            skLineSegment(sketch, "E624", {"start": v(-1124.68, 190) * mm, "end": v(-1124.68, 0) * mm, "construction": true});
            skLineSegment(sketch, "E625", {"start": v(-1124.68, 0) * mm, "end": v(-834.68, 0) * mm, "construction": true});
            skLineSegment(sketch, "E626", {"start": v(-834.68, 0) * mm, "end": v(-834.68, 190) * mm, "construction": true});
            skLineSegment(sketch, "E627", {"start": v(-834.68, 190) * mm, "end": v(-1124.68, 190) * mm, "construction": true});
            skLineSegment(sketch, "E628", {"start": v(-937.18, 152.5) * mm, "end": v(-937.18, 37.5) * mm});
            skLineSegment(sketch, "E629", {"start": v(-937.18, 37.5) * mm, "end": v(-869.68, 37.5) * mm});
            skLineSegment(sketch, "E630", {"start": v(-869.68, 37.5) * mm, "end": v(-869.68, 152.5) * mm});
            skLineSegment(sketch, "E631", {"start": v(-869.68, 152.5) * mm, "end": v(-937.18, 152.5) * mm});
            skLineSegment(sketch, "E632", {"start": v(-734.68, 190) * mm, "end": v(-734.68, 0) * mm, "construction": true});
            skLineSegment(sketch, "E633", {"start": v(-734.68, 0) * mm, "end": v(-444.68, 0) * mm, "construction": true});
            skLineSegment(sketch, "E634", {"start": v(-444.68, 0) * mm, "end": v(-444.68, 190) * mm, "construction": true});
            skLineSegment(sketch, "E635", {"start": v(-444.68, 190) * mm, "end": v(-734.68, 190) * mm, "construction": true});
            skLineSegment(sketch, "E636", {"start": v(-585.68, 152.5) * mm, "end": v(-585.68, 37.5) * mm});
            skLineSegment(sketch, "E637", {"start": v(-585.68, 37.5) * mm, "end": v(-479.68, 37.5) * mm});
            skLineSegment(sketch, "E638", {"start": v(-479.68, 37.5) * mm, "end": v(-479.68, 152.5) * mm});
            skLineSegment(sketch, "E639", {"start": v(-479.68, 152.5) * mm, "end": v(-585.68, 152.5) * mm});
            skPoint(sketch, "E640.0", {"position": v(-734.68, 0) * mm});
            skSolve(sketch);
        }
        {
            var Q0;
            Q0 = qSketchRegion(id + "F6", true);
            var Q1;
            Q1=makeQuery(id+"F6.imprint","IMPRINT",FACE,{"disambiguationData":[TD([[makeQuery(id+"F6.imprint","IMPRINT",EDGE,{"derivedFrom":sQuery(id+"F6.wireOp",EDGE,"E628")}),1.0]])]});
            extrude(context, id + "F7", {"entities" : qUnion([Q0, Q1]), "operationType" : NewBodyOperationType.REMOVE, "oppositeDirection" : true, "depth" : 88 * mm});
        }
        {
            var Q0;
            Q0=makeQuery(id+"F3.opExtrude","SWEPT_FACE",FACE,{"disambiguationData":[OSD([sQuery(id+"F2.wireOp",EDGE,"E537")])]});
            var sketch = newSketch(context, id + "F8", { "sketchPlane" : qUnion([Q0])});
            skLineSegment(sketch, "E641", {"start": v(-151.3, 181) * mm, "end": v(-151.3, 163) * mm});
            skLineSegment(sketch, "E642", {"start": v(-151.3, 163) * mm, "end": v(-120.3, 163) * mm});
            skLineSegment(sketch, "E643", {"start": v(-120.3, 163) * mm, "end": v(-120.3, 181) * mm});
            skLineSegment(sketch, "E644", {"start": v(-120.3, 181) * mm, "end": v(-151.3, 181) * mm});
            skLineSegment(sketch, "E645", {"start": v(-177.3, 155) * mm, "end": v(-177.3, 120.33) * mm});
            skLineSegment(sketch, "E646", {"start": v(-177.3, 120.33) * mm, "end": v(-159.3, 120.33) * mm});
            skLineSegment(sketch, "E647", {"start": v(-159.3, 120.33) * mm, "end": v(-159.3, 155) * mm});
            skLineSegment(sketch, "E648", {"start": v(-159.3, 155) * mm, "end": v(-177.3, 155) * mm});
            skLineSegment(sketch, "E649", {"start": v(-186.3, 190) * mm, "end": v(-186.3, 0) * mm});
            skLineSegment(sketch, "E650", {"start": v(-186.3, 0) * mm, "end": v(-46.3, 0) * mm});
            skLineSegment(sketch, "E651", {"start": v(-46.3, 0) * mm, "end": v(-46.3, 190) * mm});
            skLineSegment(sketch, "E652", {"start": v(-46.3, 190) * mm, "end": v(-186.3, 190) * mm});
            skLineSegment(sketch, "E653", {"start": v(-112.3, 181) * mm, "end": v(-112.3, 163) * mm});
            skLineSegment(sketch, "E654", {"start": v(-112.3, 163) * mm, "end": v(-81.3, 163) * mm});
            skLineSegment(sketch, "E655", {"start": v(-81.3, 163) * mm, "end": v(-81.3, 181) * mm});
            skLineSegment(sketch, "E656", {"start": v(-81.3, 181) * mm, "end": v(-112.3, 181) * mm});
            skLineSegment(sketch, "E657", {"start": v(-151.3, 27) * mm, "end": v(-151.3, 9) * mm});
            skLineSegment(sketch, "E658", {"start": v(-151.3, 9) * mm, "end": v(-120.3, 9) * mm});
            skLineSegment(sketch, "E659", {"start": v(-120.3, 9) * mm, "end": v(-120.3, 27) * mm});
            skLineSegment(sketch, "E660", {"start": v(-120.3, 27) * mm, "end": v(-151.3, 27) * mm});
            skLineSegment(sketch, "E661", {"start": v(-112.3, 27) * mm, "end": v(-112.3, 9) * mm});
            skLineSegment(sketch, "E662", {"start": v(-112.3, 9) * mm, "end": v(-81.3, 9) * mm});
            skLineSegment(sketch, "E663", {"start": v(-81.3, 9) * mm, "end": v(-81.3, 27) * mm});
            skLineSegment(sketch, "E664", {"start": v(-81.3, 27) * mm, "end": v(-112.3, 27) * mm});
            skLineSegment(sketch, "E665", {"start": v(-177.3, 112.33) * mm, "end": v(-177.3, 77.67) * mm});
            skLineSegment(sketch, "E666", {"start": v(-177.3, 77.67) * mm, "end": v(-159.3, 77.67) * mm});
            skLineSegment(sketch, "E667", {"start": v(-159.3, 77.67) * mm, "end": v(-159.3, 112.33) * mm});
            skLineSegment(sketch, "E668", {"start": v(-159.3, 112.33) * mm, "end": v(-177.3, 112.33) * mm});
            skLineSegment(sketch, "E669", {"start": v(-177.3, 69.67) * mm, "end": v(-177.3, 35) * mm});
            skLineSegment(sketch, "E670", {"start": v(-177.3, 35) * mm, "end": v(-159.3, 35) * mm});
            skLineSegment(sketch, "E671", {"start": v(-159.3, 35) * mm, "end": v(-159.3, 69.67) * mm});
            skLineSegment(sketch, "E672", {"start": v(-159.3, 69.67) * mm, "end": v(-177.3, 69.67) * mm});
            skLineSegment(sketch, "E673", {"start": v(-73.3, 155) * mm, "end": v(-73.3, 120.33) * mm});
            skLineSegment(sketch, "E674", {"start": v(-73.3, 120.33) * mm, "end": v(-55.3, 120.33) * mm});
            skLineSegment(sketch, "E675", {"start": v(-55.3, 120.33) * mm, "end": v(-55.3, 155) * mm});
            skLineSegment(sketch, "E676", {"start": v(-55.3, 155) * mm, "end": v(-73.3, 155) * mm});
            skLineSegment(sketch, "E677", {"start": v(-73.3, 112.33) * mm, "end": v(-73.3, 77.67) * mm});
            skLineSegment(sketch, "E678", {"start": v(-73.3, 77.67) * mm, "end": v(-55.3, 77.67) * mm});
            skLineSegment(sketch, "E679", {"start": v(-55.3, 77.67) * mm, "end": v(-55.3, 112.33) * mm});
            skLineSegment(sketch, "E680", {"start": v(-55.3, 112.33) * mm, "end": v(-73.3, 112.33) * mm});
            skLineSegment(sketch, "E681", {"start": v(-73.3, 69.67) * mm, "end": v(-73.3, 35) * mm});
            skLineSegment(sketch, "E682", {"start": v(-73.3, 35) * mm, "end": v(-55.3, 35) * mm});
            skLineSegment(sketch, "E683", {"start": v(-55.3, 35) * mm, "end": v(-55.3, 69.67) * mm});
            skLineSegment(sketch, "E684", {"start": v(-55.3, 69.67) * mm, "end": v(-73.3, 69.67) * mm});
            skLineSegment(sketch, "E685", {"start": v(-151.3, 155) * mm, "end": v(-151.3, 35) * mm});
            skLineSegment(sketch, "E686", {"start": v(-151.3, 35) * mm, "end": v(-81.3, 35) * mm});
            skLineSegment(sketch, "E687", {"start": v(-81.3, 35) * mm, "end": v(-81.3, 155) * mm});
            skLineSegment(sketch, "E688", {"start": v(-81.3, 155) * mm, "end": v(-151.3, 155) * mm});
            skLineSegment(sketch, "E689", {"start": v(-1108.86, 100) * mm, "end": v(-1087.27, 100) * mm});
            skLineSegment(sketch, "E690", {"start": v(-1087.27, 100) * mm, "end": v(-1083.86, 25) * mm});
            skLineSegment(sketch, "E691", {"start": v(-1083.86, 25) * mm, "end": v(-993.86, 25) * mm});
            skLineSegment(sketch, "E692", {"start": v(-993.86, 25) * mm, "end": v(-990.45, 100) * mm});
            skLineSegment(sketch, "E693", {"start": v(-990.45, 100) * mm, "end": v(-968.86, 100) * mm});
            skLineSegment(sketch, "E694", {"start": v(-968.86, 100) * mm, "end": v(-968.86, 0) * mm});
            skLineSegment(sketch, "E695", {"start": v(-968.86, 0) * mm, "end": v(-1108.86, 0) * mm});
            skLineSegment(sketch, "E696", {"start": v(-1108.86, 0) * mm, "end": v(-1108.86, 100) * mm});
            skLineSegment(sketch, "E697", {"start": v(-510.21, 193.52) * mm, "end": v(-510.21, 3.52) * mm});
            skLineSegment(sketch, "E698", {"start": v(-510.21, 3.52) * mm, "end": v(-650.21, 3.52) * mm});
            skLineSegment(sketch, "E699", {"start": v(-650.21, 3.52) * mm, "end": v(-650.21, 103.52) * mm});
            skLineSegment(sketch, "E700", {"start": v(-650.21, 103.52) * mm, "end": v(-628.62, 103.52) * mm});
            skLineSegment(sketch, "E701", {"start": v(-628.62, 103.52) * mm, "end": v(-625.21, 28.52) * mm});
            skLineSegment(sketch, "E702", {"start": v(-625.21, 28.52) * mm, "end": v(-535.21, 28.52) * mm});
            skLineSegment(sketch, "E703", {"start": v(-535.21, 28.52) * mm, "end": v(-527.71, 193.52) * mm});
            skLineSegment(sketch, "E704", {"start": v(-527.71, 193.52) * mm, "end": v(-510.21, 193.52) * mm});
            skLineSegment(sketch, "E705", {"start": v(-414.61, 193.84) * mm, "end": v(-397.11, 193.84) * mm});
            skLineSegment(sketch, "E706", {"start": v(-397.11, 193.84) * mm, "end": v(-389.61, 28.84) * mm});
            skLineSegment(sketch, "E707", {"start": v(-389.61, 28.84) * mm, "end": v(-299.61, 28.84) * mm});
            skLineSegment(sketch, "E708", {"start": v(-299.61, 28.84) * mm, "end": v(-292.11, 193.84) * mm});
            skLineSegment(sketch, "E709", {"start": v(-292.11, 193.84) * mm, "end": v(-274.61, 193.84) * mm});
            skLineSegment(sketch, "E710", {"start": v(-274.61, 193.84) * mm, "end": v(-274.61, 3.84) * mm});
            skLineSegment(sketch, "E711", {"start": v(-274.61, 3.84) * mm, "end": v(-414.61, 3.84) * mm});
            skLineSegment(sketch, "E712", {"start": v(-414.61, 3.84) * mm, "end": v(-414.61, 193.84) * mm});
            skArc(sketch, "E713.cCircle", {"start": v(-73.3, 18) * mm, "mid": v(-57.94, 11.64) * mm, "end": v(-64.3, 27) * mm});
            skPoint(sketch, "E713.cCircle.centerSnap0", {"position": v(-64.3, 35) * mm});
            skPoint(sketch, "E713.cCircle.centerSnap1", {"position": v(-81.3, 18) * mm});
            skLineSegment(sketch, "E713.0", {"start": v(-73.3, 27) * mm, "end": v(-64.3, 27) * mm});
            skLineSegment(sketch, "E713.3", {"start": v(-73.3, 18) * mm, "end": v(-73.3, 27) * mm});
            skPoint(sketch, "E713.0.midPoint", {"position": v(-64.3, 27) * mm});
            skArc(sketch, "E714.cCircle", {"start": v(-64.3, 163) * mm, "mid": v(-57.94, 178.36) * mm, "end": v(-73.3, 172) * mm});
            skPoint(sketch, "E714.cCircle.centerSnap0", {"position": v(-64.3, 155) * mm});
            skPoint(sketch, "E714.cCircle.centerSnap1", {"position": v(-81.3, 172) * mm});
            skLineSegment(sketch, "E714.0", {"start": v(-64.3, 163) * mm, "end": v(-73.3, 163) * mm});
            skLineSegment(sketch, "E714.1", {"start": v(-73.3, 163) * mm, "end": v(-73.3, 172) * mm});
            skPoint(sketch, "E714.0.midPoint", {"position": v(-64.3, 163) * mm});
            skArc(sketch, "E715.cCircle", {"start": v(-159.3, 172) * mm, "mid": v(-174.67, 178.36) * mm, "end": v(-168.3, 163) * mm});
            skPoint(sketch, "E715.cCircle.centerSnap0", {"position": v(-168.3, 155) * mm});
            skPoint(sketch, "E715.cCircle.centerSnap1", {"position": v(-151.3, 172) * mm});
            skLineSegment(sketch, "E715.0", {"start": v(-159.3, 163) * mm, "end": v(-168.3, 163) * mm});
            skLineSegment(sketch, "E715.3", {"start": v(-159.3, 172) * mm, "end": v(-159.3, 163) * mm});
            skPoint(sketch, "E715.0.midPoint", {"position": v(-168.3, 163) * mm});
            skArc(sketch, "E716.cCircle", {"start": v(-168.3, 27) * mm, "mid": v(-174.67, 11.64) * mm, "end": v(-159.3, 18) * mm});
            skPoint(sketch, "E716.cCircle.centerSnap0", {"position": v(-168.3, 35) * mm});
            skPoint(sketch, "E716.cCircle.centerSnap1", {"position": v(-151.3, 18) * mm});
            skLineSegment(sketch, "E716.0", {"start": v(-168.3, 27) * mm, "end": v(-159.3, 27) * mm});
            skLineSegment(sketch, "E716.1", {"start": v(-159.3, 27) * mm, "end": v(-159.3, 18) * mm});
            skPoint(sketch, "E716.0.midPoint", {"position": v(-168.3, 27) * mm});
            skPoint(sketch, "E717.orphan", {"position": v(-55.3, 163) * mm});
            skPoint(sketch, "E718.orphan", {"position": v(-159.3, 181) * mm});
            skPoint(sketch, "E719.orphan", {"position": v(-177.3, 163) * mm});
            skPoint(sketch, "E720.orphan", {"position": v(-177.3, 27) * mm});
            skPoint(sketch, "E721.orphan", {"position": v(-55.3, 27) * mm});
            skPoint(sketch, "E722.orphan", {"position": v(-73.3, 9) * mm});
            skLineSegment(sketch, "E723", {"start": v(-858.9, 153.52) * mm, "end": v(-853.21, 28.52) * mm});
            skLineSegment(sketch, "E724", {"start": v(-853.21, 28.52) * mm, "end": v(-763.21, 28.52) * mm});
            skLineSegment(sketch, "E725", {"start": v(-763.21, 28.52) * mm, "end": v(-755.71, 193.52) * mm});
            skLineSegment(sketch, "E726", {"start": v(-755.71, 193.52) * mm, "end": v(-738.21, 193.52) * mm});
            skLineSegment(sketch, "E727", {"start": v(-738.21, 193.52) * mm, "end": v(-738.21, 3.52) * mm});
            skLineSegment(sketch, "E728", {"start": v(-738.21, 3.52) * mm, "end": v(-878.21, 3.52) * mm});
            skLineSegment(sketch, "E729", {"start": v(-878.21, 3.52) * mm, "end": v(-878.21, 153.52) * mm});
            skLineSegment(sketch, "E730", {"start": v(-858.9, 153.52) * mm, "end": v(-878.21, 153.52) * mm});
            skSolve(sketch);
        }
        {
            var Q0;
            Q0 = qSketchRegion(id + "F8", true);
            extrude(context, id + "F9", {"entities" : qUnion([Q0]), "oppositeDirection" : true, "depth" : 290 * mm});
        }
    });
